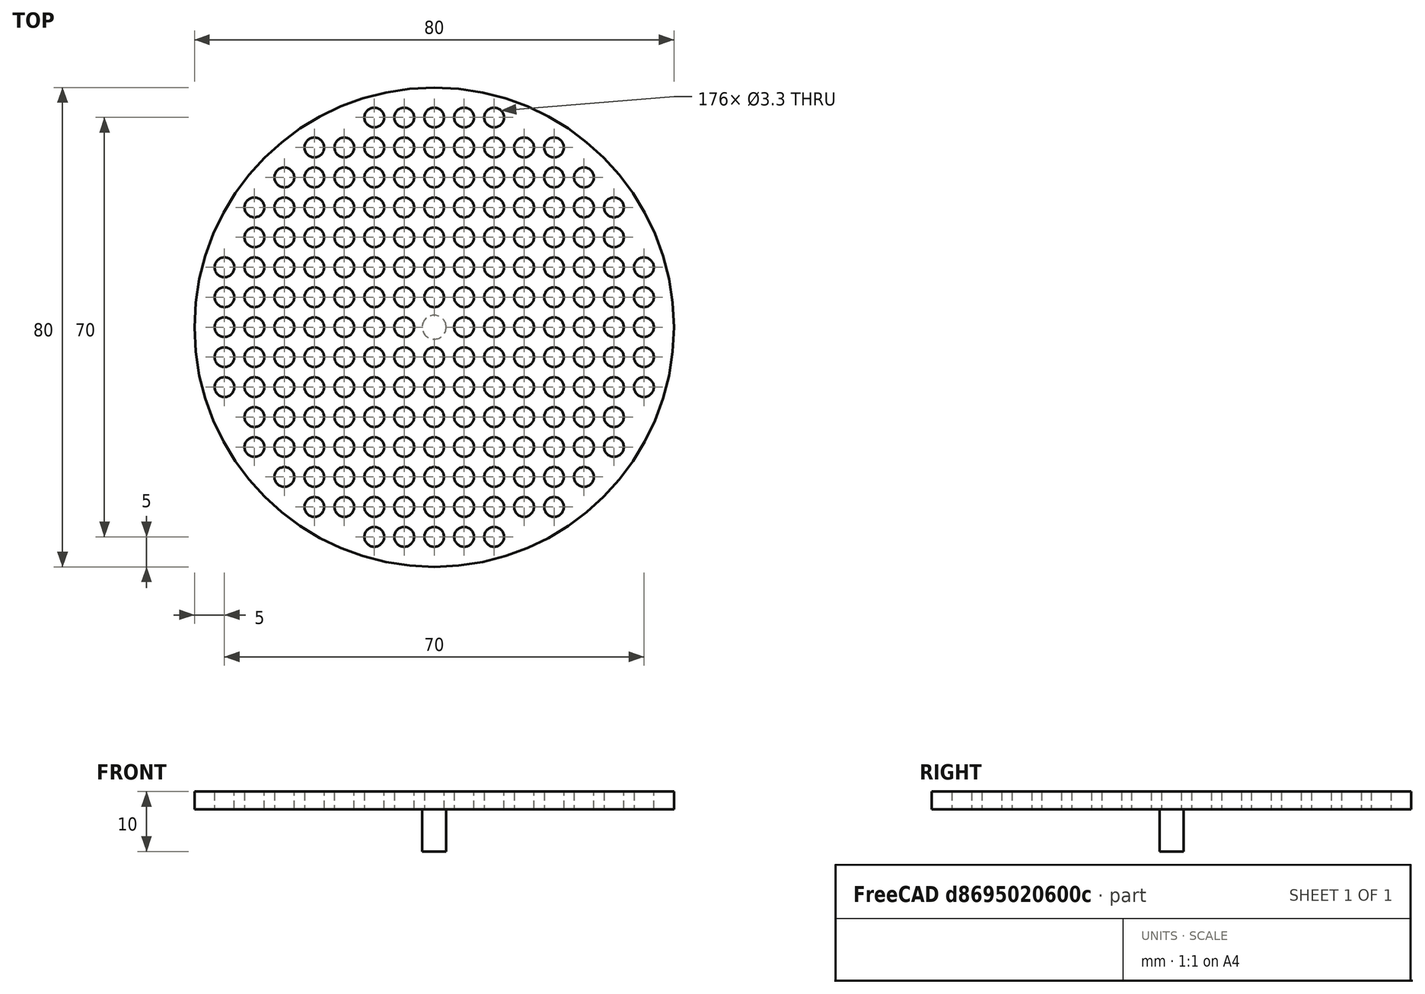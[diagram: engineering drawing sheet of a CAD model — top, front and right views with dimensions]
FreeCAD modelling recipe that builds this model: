
FCSTD DOCUMENT  (FreeCAD 0.21R0.21.2)
Label: XL30SampleholderBreadboard_D80
License: All rights reserved
LicenseURL: https://en.wikipedia.org/wiki/All_rights_reserved
objects: Part::Cylinder×178, Part::MultiFuse×17, TechDraw::DrawViewDimension×7, TechDraw::DrawProjGroupItem×3, Spreadsheet::Sheet×1, Part::Cut×1, TechDraw::DrawSVGTemplate×1, TechDraw::DrawProjGroup×1, TechDraw::DrawPage×1
note: 205 computed .brp shape members not serialized (recipe doc carries the construction recipe); baked Part::Feature solids carry a one-line shape summary decoded from their .brp

FEATURE [Spreadsheet::Sheet] Spreadsheet  label="BreadboardConfig"
  cells = A1='Parameters; A2='Diameter of stage; B2(dia_breadboard)=80; C2='The outer diameter of the breadboard stage; A3='Corehole diameter; B3(screw_corehole)=3.3; C3='Corehole diameter for screws (3.3mm for M4); A4='Plate thickness; B4(t_plate)=3; A5='Hole spacing; B5(screw_spacing)=5
FEATURE [Part::Cylinder] Cylinder
  Angle = 360
  AttacherType = Attacher::AttachEngine3D
  FirstAngle = 0
  Height = 7
  Placement = pos=(0,0,-7) rot=(0,0,1;0rad)
  Radius = 2
  SecondAngle = 0
FEATURE [Part::Cylinder] Cylinder001
  Angle = 360
  AttacherType = Attacher::AttachEngine3D
  FirstAngle = 0
  Height = 3
  Radius = 40
  SecondAngle = 0
  expr: Height = <<BreadboardConfig>>.t_plate
  expr: Radius = <<BreadboardConfig>>.dia_breadboard / 2
FEATURE [Part::MultiFuse] Fusion
  Shapes = -> [Cylinder,Cylinder001]
FEATURE [Part::Cylinder] Cylinder002
  Angle = 360
  AttacherType = Attacher::AttachEngine3D
  FirstAngle = 0
  Height = 3
  Placement = pos=(5,0,0) rot=(0,0,1;0rad)
  Radius = 1.65
  SecondAngle = 0
  expr: .Placement.Base.x = <<BreadboardConfig>>.screw_spacing * 1
  expr: Height = <<BreadboardConfig>>.t_plate
  expr: Radius = <<BreadboardConfig>>.screw_corehole / 2
FEATURE [Part::Cylinder] Cylinder003
  Angle = 360
  AttacherType = Attacher::AttachEngine3D
  FirstAngle = 0
  Height = 3
  Placement = pos=(10,0,0) rot=(0,0,1;0rad)
  Radius = 1.65
  SecondAngle = 0
  expr: .Placement.Base.x = <<BreadboardConfig>>.screw_spacing * 2
  expr: Height = <<BreadboardConfig>>.t_plate
  expr: Radius = <<BreadboardConfig>>.screw_corehole / 2
FEATURE [Part::Cylinder] Cylinder004
  Angle = 360
  AttacherType = Attacher::AttachEngine3D
  FirstAngle = 0
  Height = 3
  Placement = pos=(15,0,0) rot=(0,0,1;0rad)
  Radius = 1.65
  SecondAngle = 0
  expr: .Placement.Base.x = <<BreadboardConfig>>.screw_spacing * 3
  expr: Height = <<BreadboardConfig>>.t_plate
  expr: Radius = <<BreadboardConfig>>.screw_corehole / 2
FEATURE [Part::Cylinder] Cylinder005
  Angle = 360
  AttacherType = Attacher::AttachEngine3D
  FirstAngle = 0
  Height = 3
  Placement = pos=(20,0,0) rot=(0,0,1;0rad)
  Radius = 1.65
  SecondAngle = 0
  expr: .Placement.Base.x = <<BreadboardConfig>>.screw_spacing * 4
  expr: Height = <<BreadboardConfig>>.t_plate
  expr: Radius = <<BreadboardConfig>>.screw_corehole / 2
FEATURE [Part::Cylinder] Cylinder006
  Angle = 360
  AttacherType = Attacher::AttachEngine3D
  FirstAngle = 0
  Height = 3
  Placement = pos=(25,0,0) rot=(0,0,1;0rad)
  Radius = 1.65
  SecondAngle = 0
  expr: .Placement.Base.x = <<BreadboardConfig>>.screw_spacing * 5
  expr: Height = <<BreadboardConfig>>.t_plate
  expr: Radius = <<BreadboardConfig>>.screw_corehole / 2
FEATURE [Part::Cylinder] Cylinder007
  Angle = 360
  AttacherType = Attacher::AttachEngine3D
  FirstAngle = 0
  Height = 3
  Placement = pos=(30,0,0) rot=(0,0,1;0rad)
  Radius = 1.65
  SecondAngle = 0
  expr: .Placement.Base.x = <<BreadboardConfig>>.screw_spacing * 6
  expr: Height = <<BreadboardConfig>>.t_plate
  expr: Radius = <<BreadboardConfig>>.screw_corehole / 2
FEATURE [Part::Cylinder] Cylinder008
  Angle = 360
  AttacherType = Attacher::AttachEngine3D
  FirstAngle = 0
  Height = 3
  Placement = pos=(35,0,0) rot=(0,0,1;0rad)
  Radius = 1.65
  SecondAngle = 0
  expr: .Placement.Base.x = <<BreadboardConfig>>.screw_spacing * 7
  expr: Height = <<BreadboardConfig>>.t_plate
  expr: Radius = <<BreadboardConfig>>.screw_corehole / 2
FEATURE [Part::Cylinder] Cylinder012
  Angle = 360
  AttacherType = Attacher::AttachEngine3D
  FirstAngle = 0
  Height = 3
  Placement = pos=(-5,0,0) rot=(0,0,1;0rad)
  Radius = 1.65
  SecondAngle = 0
  expr: .Placement.Base.x = <<BreadboardConfig>>.screw_spacing * -1
  expr: Height = <<BreadboardConfig>>.t_plate
  expr: Radius = <<BreadboardConfig>>.screw_corehole / 2
FEATURE [Part::Cylinder] Cylinder013
  Angle = 360
  AttacherType = Attacher::AttachEngine3D
  FirstAngle = 0
  Height = 3
  Placement = pos=(-10,0,0) rot=(0,0,1;0rad)
  Radius = 1.65
  SecondAngle = 0
  expr: .Placement.Base.x = <<BreadboardConfig>>.screw_spacing * -2
  expr: Height = <<BreadboardConfig>>.t_plate
  expr: Radius = <<BreadboardConfig>>.screw_corehole / 2
FEATURE [Part::Cylinder] Cylinder014
  Angle = 360
  AttacherType = Attacher::AttachEngine3D
  FirstAngle = 0
  Height = 3
  Placement = pos=(-15,0,0) rot=(0,0,1;0rad)
  Radius = 1.65
  SecondAngle = 0
  expr: .Placement.Base.x = <<BreadboardConfig>>.screw_spacing * -3
  expr: Height = <<BreadboardConfig>>.t_plate
  expr: Radius = <<BreadboardConfig>>.screw_corehole / 2
FEATURE [Part::Cylinder] Cylinder015
  Angle = 360
  AttacherType = Attacher::AttachEngine3D
  FirstAngle = 0
  Height = 3
  Placement = pos=(-20,0,0) rot=(0,0,1;0rad)
  Radius = 1.65
  SecondAngle = 0
  expr: .Placement.Base.x = <<BreadboardConfig>>.screw_spacing * -4
  expr: Height = <<BreadboardConfig>>.t_plate
  expr: Radius = <<BreadboardConfig>>.screw_corehole / 2
FEATURE [Part::Cylinder] Cylinder016
  Angle = 360
  AttacherType = Attacher::AttachEngine3D
  FirstAngle = 0
  Height = 3
  Placement = pos=(-25,0,0) rot=(0,0,1;0rad)
  Radius = 1.65
  SecondAngle = 0
  expr: .Placement.Base.x = <<BreadboardConfig>>.screw_spacing * -5
  expr: Height = <<BreadboardConfig>>.t_plate
  expr: Radius = <<BreadboardConfig>>.screw_corehole / 2
FEATURE [Part::Cylinder] Cylinder017
  Angle = 360
  AttacherType = Attacher::AttachEngine3D
  FirstAngle = 0
  Height = 3
  Placement = pos=(-30,0,0) rot=(0,0,1;0rad)
  Radius = 1.65
  SecondAngle = 0
  expr: .Placement.Base.x = <<BreadboardConfig>>.screw_spacing * -6
  expr: Height = <<BreadboardConfig>>.t_plate
  expr: Radius = <<BreadboardConfig>>.screw_corehole / 2
FEATURE [Part::Cylinder] Cylinder018
  Angle = 360
  AttacherType = Attacher::AttachEngine3D
  FirstAngle = 0
  Height = 3
  Placement = pos=(-35,0,0) rot=(0,0,1;0rad)
  Radius = 1.65
  SecondAngle = 0
  expr: .Placement.Base.x = <<BreadboardConfig>>.screw_spacing * -7
  expr: Height = <<BreadboardConfig>>.t_plate
  expr: Radius = <<BreadboardConfig>>.screw_corehole / 2
FEATURE [Part::MultiFuse] Fusion001
  Shapes = -> [Cylinder018,Cylinder017,Cylinder016,Cylinder015,Cylinder014,Cylinder013,Cylinder012,Cylinder008,Cylinder007,Cylinder006,Cylinder005,Cylinder004,Cylinder003,Cylinder002]
FEATURE [Part::Cylinder] Cylinder022
  Angle = 360
  AttacherType = Attacher::AttachEngine3D
  FirstAngle = 0
  Height = 3
  Placement = pos=(5,0,0) rot=(0,0,1;0rad)
  Radius = 1.65
  SecondAngle = 0
  expr: .Placement.Base.x = <<BreadboardConfig>>.screw_spacing * 1
  expr: Height = <<BreadboardConfig>>.t_plate
  expr: Radius = <<BreadboardConfig>>.screw_corehole / 2
FEATURE [Part::Cylinder] Cylinder023
  Angle = 360
  AttacherType = Attacher::AttachEngine3D
  FirstAngle = 0
  Height = 3
  Placement = pos=(10,0,0) rot=(0,0,1;0rad)
  Radius = 1.65
  SecondAngle = 0
  expr: .Placement.Base.x = <<BreadboardConfig>>.screw_spacing * 2
  expr: Height = <<BreadboardConfig>>.t_plate
  expr: Radius = <<BreadboardConfig>>.screw_corehole / 2
FEATURE [Part::Cylinder] Cylinder024
  Angle = 360
  AttacherType = Attacher::AttachEngine3D
  FirstAngle = 0
  Height = 3
  Placement = pos=(15,0,0) rot=(0,0,1;0rad)
  Radius = 1.65
  SecondAngle = 0
  expr: .Placement.Base.x = <<BreadboardConfig>>.screw_spacing * 3
  expr: Height = <<BreadboardConfig>>.t_plate
  expr: Radius = <<BreadboardConfig>>.screw_corehole / 2
FEATURE [Part::Cylinder] Cylinder032
  Angle = 360
  AttacherType = Attacher::AttachEngine3D
  FirstAngle = 0
  Height = 3
  Placement = pos=(-5,0,0) rot=(0,0,1;0rad)
  Radius = 1.65
  SecondAngle = 0
  expr: .Placement.Base.x = <<BreadboardConfig>>.screw_spacing * -1
  expr: Height = <<BreadboardConfig>>.t_plate
  expr: Radius = <<BreadboardConfig>>.screw_corehole / 2
FEATURE [Part::Cylinder] Cylinder033
  Angle = 360
  AttacherType = Attacher::AttachEngine3D
  FirstAngle = 0
  Height = 3
  Placement = pos=(-10,0,0) rot=(0,0,1;0rad)
  Radius = 1.65
  SecondAngle = 0
  expr: .Placement.Base.x = <<BreadboardConfig>>.screw_spacing * -2
  expr: Height = <<BreadboardConfig>>.t_plate
  expr: Radius = <<BreadboardConfig>>.screw_corehole / 2
FEATURE [Part::Cylinder] Cylinder034
  Angle = 360
  AttacherType = Attacher::AttachEngine3D
  FirstAngle = 0
  Height = 3
  Placement = pos=(-15,0,0) rot=(0,0,1;0rad)
  Radius = 1.65
  SecondAngle = 0
  expr: .Placement.Base.x = <<BreadboardConfig>>.screw_spacing * -3
  expr: Height = <<BreadboardConfig>>.t_plate
  expr: Radius = <<BreadboardConfig>>.screw_corehole / 2
FEATURE [Part::Cylinder] Cylinder042
  Angle = 360
  AttacherType = Attacher::AttachEngine3D
  FirstAngle = 0
  Height = 3
  Radius = 1.65
  SecondAngle = 0
  expr: Height = <<BreadboardConfig>>.t_plate
  expr: Radius = <<BreadboardConfig>>.screw_corehole / 2
FEATURE [Part::Cylinder] Cylinder043
  Angle = 360
  AttacherType = Attacher::AttachEngine3D
  FirstAngle = 0
  Height = 3
  Placement = pos=(5,0,0) rot=(0,0,1;0rad)
  Radius = 1.65
  SecondAngle = 0
  expr: .Placement.Base.x = <<BreadboardConfig>>.screw_spacing * 1
  expr: Height = <<BreadboardConfig>>.t_plate
  expr: Radius = <<BreadboardConfig>>.screw_corehole / 2
FEATURE [Part::Cylinder] Cylinder044
  Angle = 360
  AttacherType = Attacher::AttachEngine3D
  FirstAngle = 0
  Height = 3
  Placement = pos=(10,0,0) rot=(0,0,1;0rad)
  Radius = 1.65
  SecondAngle = 0
  expr: .Placement.Base.x = <<BreadboardConfig>>.screw_spacing * 2
  expr: Height = <<BreadboardConfig>>.t_plate
  expr: Radius = <<BreadboardConfig>>.screw_corehole / 2
FEATURE [Part::Cylinder] Cylinder045
  Angle = 360
  AttacherType = Attacher::AttachEngine3D
  FirstAngle = 0
  Height = 3
  Placement = pos=(15,0,0) rot=(0,0,1;0rad)
  Radius = 1.65
  SecondAngle = 0
  expr: .Placement.Base.x = <<BreadboardConfig>>.screw_spacing * 3
  expr: Height = <<BreadboardConfig>>.t_plate
  expr: Radius = <<BreadboardConfig>>.screw_corehole / 2
FEATURE [Part::Cylinder] Cylinder046
  Angle = 360
  AttacherType = Attacher::AttachEngine3D
  FirstAngle = 0
  Height = 3
  Placement = pos=(20,0,0) rot=(0,0,1;0rad)
  Radius = 1.65
  SecondAngle = 0
  expr: .Placement.Base.x = <<BreadboardConfig>>.screw_spacing * 4
  expr: Height = <<BreadboardConfig>>.t_plate
  expr: Radius = <<BreadboardConfig>>.screw_corehole / 2
FEATURE [Part::Cylinder] Cylinder047
  Angle = 360
  AttacherType = Attacher::AttachEngine3D
  FirstAngle = 0
  Height = 3
  Placement = pos=(25,0,0) rot=(0,0,1;0rad)
  Radius = 1.65
  SecondAngle = 0
  expr: .Placement.Base.x = <<BreadboardConfig>>.screw_spacing * 5
  expr: Height = <<BreadboardConfig>>.t_plate
  expr: Radius = <<BreadboardConfig>>.screw_corehole / 2
FEATURE [Part::Cylinder] Cylinder048
  Angle = 360
  AttacherType = Attacher::AttachEngine3D
  FirstAngle = 0
  Height = 3
  Placement = pos=(30,0,0) rot=(0,0,1;0rad)
  Radius = 1.65
  SecondAngle = 0
  expr: .Placement.Base.x = <<BreadboardConfig>>.screw_spacing * 6
  expr: Height = <<BreadboardConfig>>.t_plate
  expr: Radius = <<BreadboardConfig>>.screw_corehole / 2
FEATURE [Part::Cylinder] Cylinder049
  Angle = 360
  AttacherType = Attacher::AttachEngine3D
  FirstAngle = 0
  Height = 3
  Placement = pos=(35,0,0) rot=(0,0,1;0rad)
  Radius = 1.65
  SecondAngle = 0
  expr: .Placement.Base.x = <<BreadboardConfig>>.screw_spacing * 7
  expr: Height = <<BreadboardConfig>>.t_plate
  expr: Radius = <<BreadboardConfig>>.screw_corehole / 2
FEATURE [Part::Cylinder] Cylinder053
  Angle = 360
  AttacherType = Attacher::AttachEngine3D
  FirstAngle = 0
  Height = 3
  Placement = pos=(-5,0,0) rot=(0,0,1;0rad)
  Radius = 1.65
  SecondAngle = 0
  expr: .Placement.Base.x = <<BreadboardConfig>>.screw_spacing * -1
  expr: Height = <<BreadboardConfig>>.t_plate
  expr: Radius = <<BreadboardConfig>>.screw_corehole / 2
FEATURE [Part::Cylinder] Cylinder054
  Angle = 360
  AttacherType = Attacher::AttachEngine3D
  FirstAngle = 0
  Height = 3
  Placement = pos=(-10,0,0) rot=(0,0,1;0rad)
  Radius = 1.65
  SecondAngle = 0
  expr: .Placement.Base.x = <<BreadboardConfig>>.screw_spacing * -2
  expr: Height = <<BreadboardConfig>>.t_plate
  expr: Radius = <<BreadboardConfig>>.screw_corehole / 2
FEATURE [Part::Cylinder] Cylinder055
  Angle = 360
  AttacherType = Attacher::AttachEngine3D
  FirstAngle = 0
  Height = 3
  Placement = pos=(-15,0,0) rot=(0,0,1;0rad)
  Radius = 1.65
  SecondAngle = 0
  expr: .Placement.Base.x = <<BreadboardConfig>>.screw_spacing * -3
  expr: Height = <<BreadboardConfig>>.t_plate
  expr: Radius = <<BreadboardConfig>>.screw_corehole / 2
FEATURE [Part::Cylinder] Cylinder056
  Angle = 360
  AttacherType = Attacher::AttachEngine3D
  FirstAngle = 0
  Height = 3
  Placement = pos=(-20,0,0) rot=(0,0,1;0rad)
  Radius = 1.65
  SecondAngle = 0
  expr: .Placement.Base.x = <<BreadboardConfig>>.screw_spacing * -4
  expr: Height = <<BreadboardConfig>>.t_plate
  expr: Radius = <<BreadboardConfig>>.screw_corehole / 2
FEATURE [Part::Cylinder] Cylinder057
  Angle = 360
  AttacherType = Attacher::AttachEngine3D
  FirstAngle = 0
  Height = 3
  Placement = pos=(-25,0,0) rot=(0,0,1;0rad)
  Radius = 1.65
  SecondAngle = 0
  expr: .Placement.Base.x = <<BreadboardConfig>>.screw_spacing * -5
  expr: Height = <<BreadboardConfig>>.t_plate
  expr: Radius = <<BreadboardConfig>>.screw_corehole / 2
FEATURE [Part::Cylinder] Cylinder058
  Angle = 360
  AttacherType = Attacher::AttachEngine3D
  FirstAngle = 0
  Height = 3
  Placement = pos=(-30,0,0) rot=(0,0,1;0rad)
  Radius = 1.65
  SecondAngle = 0
  expr: .Placement.Base.x = <<BreadboardConfig>>.screw_spacing * -6
  expr: Height = <<BreadboardConfig>>.t_plate
  expr: Radius = <<BreadboardConfig>>.screw_corehole / 2
FEATURE [Part::Cylinder] Cylinder059
  Angle = 360
  AttacherType = Attacher::AttachEngine3D
  FirstAngle = 0
  Height = 3
  Placement = pos=(-35,0,0) rot=(0,0,1;0rad)
  Radius = 1.65
  SecondAngle = 0
  expr: .Placement.Base.x = <<BreadboardConfig>>.screw_spacing * -7
  expr: Height = <<BreadboardConfig>>.t_plate
  expr: Radius = <<BreadboardConfig>>.screw_corehole / 2
FEATURE [Part::Cylinder] Cylinder063
  Angle = 360
  AttacherType = Attacher::AttachEngine3D
  FirstAngle = 0
  Height = 3
  Radius = 1.65
  SecondAngle = 0
  expr: Height = <<BreadboardConfig>>.t_plate
  expr: Radius = <<BreadboardConfig>>.screw_corehole / 2
FEATURE [Part::MultiFuse] Fusion003
  Placement = pos=(0,10,0) rot=(0,0,1;0rad)
  Shapes = -> [Cylinder059,Cylinder058,Cylinder057,Cylinder056,Cylinder055,Cylinder054,Cylinder053,Cylinder049,Cylinder048,Cylinder047,Cylinder046,Cylinder045,Cylinder044,Cylinder043,Cylinder063]
  expr: .Placement.Base.y = <<BreadboardConfig>>.screw_spacing * 2
FEATURE [Part::Cylinder] Cylinder064
  Angle = 360
  AttacherType = Attacher::AttachEngine3D
  FirstAngle = 0
  Height = 3
  Placement = pos=(5,0,0) rot=(0,0,1;0rad)
  Radius = 1.65
  SecondAngle = 0
  expr: .Placement.Base.x = <<BreadboardConfig>>.screw_spacing * 1
  expr: Height = <<BreadboardConfig>>.t_plate
  expr: Radius = <<BreadboardConfig>>.screw_corehole / 2
FEATURE [Part::Cylinder] Cylinder065
  Angle = 360
  AttacherType = Attacher::AttachEngine3D
  FirstAngle = 0
  Height = 3
  Placement = pos=(10,0,0) rot=(0,0,1;0rad)
  Radius = 1.65
  SecondAngle = 0
  expr: .Placement.Base.x = <<BreadboardConfig>>.screw_spacing * 2
  expr: Height = <<BreadboardConfig>>.t_plate
  expr: Radius = <<BreadboardConfig>>.screw_corehole / 2
FEATURE [Part::Cylinder] Cylinder066
  Angle = 360
  AttacherType = Attacher::AttachEngine3D
  FirstAngle = 0
  Height = 3
  Placement = pos=(15,0,0) rot=(0,0,1;0rad)
  Radius = 1.65
  SecondAngle = 0
  expr: .Placement.Base.x = <<BreadboardConfig>>.screw_spacing * 3
  expr: Height = <<BreadboardConfig>>.t_plate
  expr: Radius = <<BreadboardConfig>>.screw_corehole / 2
FEATURE [Part::Cylinder] Cylinder067
  Angle = 360
  AttacherType = Attacher::AttachEngine3D
  FirstAngle = 0
  Height = 3
  Placement = pos=(20,0,0) rot=(0,0,1;0rad)
  Radius = 1.65
  SecondAngle = 0
  expr: .Placement.Base.x = <<BreadboardConfig>>.screw_spacing * 4
  expr: Height = <<BreadboardConfig>>.t_plate
  expr: Radius = <<BreadboardConfig>>.screw_corehole / 2
FEATURE [Part::Cylinder] Cylinder068
  Angle = 360
  AttacherType = Attacher::AttachEngine3D
  FirstAngle = 0
  Height = 3
  Placement = pos=(25,0,0) rot=(0,0,1;0rad)
  Radius = 1.65
  SecondAngle = 0
  expr: .Placement.Base.x = <<BreadboardConfig>>.screw_spacing * 5
  expr: Height = <<BreadboardConfig>>.t_plate
  expr: Radius = <<BreadboardConfig>>.screw_corehole / 2
FEATURE [Part::Cylinder] Cylinder069
  Angle = 360
  AttacherType = Attacher::AttachEngine3D
  FirstAngle = 0
  Height = 3
  Placement = pos=(30,0,0) rot=(0,0,1;0rad)
  Radius = 1.65
  SecondAngle = 0
  expr: .Placement.Base.x = <<BreadboardConfig>>.screw_spacing * 6
  expr: Height = <<BreadboardConfig>>.t_plate
  expr: Radius = <<BreadboardConfig>>.screw_corehole / 2
FEATURE [Part::Cylinder] Cylinder074
  Angle = 360
  AttacherType = Attacher::AttachEngine3D
  FirstAngle = 0
  Height = 3
  Placement = pos=(-5,0,0) rot=(0,0,1;0rad)
  Radius = 1.65
  SecondAngle = 0
  expr: .Placement.Base.x = <<BreadboardConfig>>.screw_spacing * -1
  expr: Height = <<BreadboardConfig>>.t_plate
  expr: Radius = <<BreadboardConfig>>.screw_corehole / 2
FEATURE [Part::Cylinder] Cylinder075
  Angle = 360
  AttacherType = Attacher::AttachEngine3D
  FirstAngle = 0
  Height = 3
  Placement = pos=(-10,0,0) rot=(0,0,1;0rad)
  Radius = 1.65
  SecondAngle = 0
  expr: .Placement.Base.x = <<BreadboardConfig>>.screw_spacing * -2
  expr: Height = <<BreadboardConfig>>.t_plate
  expr: Radius = <<BreadboardConfig>>.screw_corehole / 2
FEATURE [Part::Cylinder] Cylinder076
  Angle = 360
  AttacherType = Attacher::AttachEngine3D
  FirstAngle = 0
  Height = 3
  Placement = pos=(-15,0,0) rot=(0,0,1;0rad)
  Radius = 1.65
  SecondAngle = 0
  expr: .Placement.Base.x = <<BreadboardConfig>>.screw_spacing * -3
  expr: Height = <<BreadboardConfig>>.t_plate
  expr: Radius = <<BreadboardConfig>>.screw_corehole / 2
FEATURE [Part::Cylinder] Cylinder077
  Angle = 360
  AttacherType = Attacher::AttachEngine3D
  FirstAngle = 0
  Height = 3
  Placement = pos=(-20,0,0) rot=(0,0,1;0rad)
  Radius = 1.65
  SecondAngle = 0
  expr: .Placement.Base.x = <<BreadboardConfig>>.screw_spacing * -4
  expr: Height = <<BreadboardConfig>>.t_plate
  expr: Radius = <<BreadboardConfig>>.screw_corehole / 2
FEATURE [Part::Cylinder] Cylinder078
  Angle = 360
  AttacherType = Attacher::AttachEngine3D
  FirstAngle = 0
  Height = 3
  Placement = pos=(-25,0,0) rot=(0,0,1;0rad)
  Radius = 1.65
  SecondAngle = 0
  expr: .Placement.Base.x = <<BreadboardConfig>>.screw_spacing * -5
  expr: Height = <<BreadboardConfig>>.t_plate
  expr: Radius = <<BreadboardConfig>>.screw_corehole / 2
FEATURE [Part::Cylinder] Cylinder079
  Angle = 360
  AttacherType = Attacher::AttachEngine3D
  FirstAngle = 0
  Height = 3
  Placement = pos=(-30,0,0) rot=(0,0,1;0rad)
  Radius = 1.65
  SecondAngle = 0
  expr: .Placement.Base.x = <<BreadboardConfig>>.screw_spacing * -6
  expr: Height = <<BreadboardConfig>>.t_plate
  expr: Radius = <<BreadboardConfig>>.screw_corehole / 2
FEATURE [Part::Cylinder] Cylinder084
  Angle = 360
  AttacherType = Attacher::AttachEngine3D
  FirstAngle = 0
  Height = 3
  Radius = 1.65
  SecondAngle = 0
  expr: Height = <<BreadboardConfig>>.t_plate
  expr: Radius = <<BreadboardConfig>>.screw_corehole / 2
FEATURE [Part::MultiFuse] Fusion004
  Placement = pos=(0,15,0) rot=(0,0,1;0rad)
  Shapes = -> [Cylinder079,Cylinder078,Cylinder077,Cylinder076,Cylinder075,Cylinder074,Cylinder069,Cylinder068,Cylinder067,Cylinder066,Cylinder065,Cylinder064,Cylinder084]
  expr: .Placement.Base.y = <<BreadboardConfig>>.screw_spacing * 3
FEATURE [Part::Cylinder] Cylinder085
  Angle = 360
  AttacherType = Attacher::AttachEngine3D
  FirstAngle = 0
  Height = 3
  Placement = pos=(5,0,0) rot=(0,0,1;0rad)
  Radius = 1.65
  SecondAngle = 0
  expr: .Placement.Base.x = <<BreadboardConfig>>.screw_spacing * 1
  expr: Height = <<BreadboardConfig>>.t_plate
  expr: Radius = <<BreadboardConfig>>.screw_corehole / 2
FEATURE [Part::Cylinder] Cylinder086
  Angle = 360
  AttacherType = Attacher::AttachEngine3D
  FirstAngle = 0
  Height = 3
  Placement = pos=(10,0,0) rot=(0,0,1;0rad)
  Radius = 1.65
  SecondAngle = 0
  expr: .Placement.Base.x = <<BreadboardConfig>>.screw_spacing * 2
  expr: Height = <<BreadboardConfig>>.t_plate
  expr: Radius = <<BreadboardConfig>>.screw_corehole / 2
FEATURE [Part::Cylinder] Cylinder087
  Angle = 360
  AttacherType = Attacher::AttachEngine3D
  FirstAngle = 0
  Height = 3
  Placement = pos=(15,0,0) rot=(0,0,1;0rad)
  Radius = 1.65
  SecondAngle = 0
  expr: .Placement.Base.x = <<BreadboardConfig>>.screw_spacing * 3
  expr: Height = <<BreadboardConfig>>.t_plate
  expr: Radius = <<BreadboardConfig>>.screw_corehole / 2
FEATURE [Part::Cylinder] Cylinder088
  Angle = 360
  AttacherType = Attacher::AttachEngine3D
  FirstAngle = 0
  Height = 3
  Placement = pos=(20,0,0) rot=(0,0,1;0rad)
  Radius = 1.65
  SecondAngle = 0
  expr: .Placement.Base.x = <<BreadboardConfig>>.screw_spacing * 4
  expr: Height = <<BreadboardConfig>>.t_plate
  expr: Radius = <<BreadboardConfig>>.screw_corehole / 2
FEATURE [Part::Cylinder] Cylinder089
  Angle = 360
  AttacherType = Attacher::AttachEngine3D
  FirstAngle = 0
  Height = 3
  Placement = pos=(25,0,0) rot=(0,0,1;0rad)
  Radius = 1.65
  SecondAngle = 0
  expr: .Placement.Base.x = <<BreadboardConfig>>.screw_spacing * 5
  expr: Height = <<BreadboardConfig>>.t_plate
  expr: Radius = <<BreadboardConfig>>.screw_corehole / 2
FEATURE [Part::Cylinder] Cylinder090
  Angle = 360
  AttacherType = Attacher::AttachEngine3D
  FirstAngle = 0
  Height = 3
  Placement = pos=(30,0,0) rot=(0,0,1;0rad)
  Radius = 1.65
  SecondAngle = 0
  expr: .Placement.Base.x = <<BreadboardConfig>>.screw_spacing * 6
  expr: Height = <<BreadboardConfig>>.t_plate
  expr: Radius = <<BreadboardConfig>>.screw_corehole / 2
FEATURE [Part::Cylinder] Cylinder095
  Angle = 360
  AttacherType = Attacher::AttachEngine3D
  FirstAngle = 0
  Height = 3
  Placement = pos=(-5,0,0) rot=(0,0,1;0rad)
  Radius = 1.65
  SecondAngle = 0
  expr: .Placement.Base.x = <<BreadboardConfig>>.screw_spacing * -1
  expr: Height = <<BreadboardConfig>>.t_plate
  expr: Radius = <<BreadboardConfig>>.screw_corehole / 2
FEATURE [Part::Cylinder] Cylinder096
  Angle = 360
  AttacherType = Attacher::AttachEngine3D
  FirstAngle = 0
  Height = 3
  Placement = pos=(-10,0,0) rot=(0,0,1;0rad)
  Radius = 1.65
  SecondAngle = 0
  expr: .Placement.Base.x = <<BreadboardConfig>>.screw_spacing * -2
  expr: Height = <<BreadboardConfig>>.t_plate
  expr: Radius = <<BreadboardConfig>>.screw_corehole / 2
FEATURE [Part::Cylinder] Cylinder097
  Angle = 360
  AttacherType = Attacher::AttachEngine3D
  FirstAngle = 0
  Height = 3
  Placement = pos=(-15,0,0) rot=(0,0,1;0rad)
  Radius = 1.65
  SecondAngle = 0
  expr: .Placement.Base.x = <<BreadboardConfig>>.screw_spacing * -3
  expr: Height = <<BreadboardConfig>>.t_plate
  expr: Radius = <<BreadboardConfig>>.screw_corehole / 2
FEATURE [Part::Cylinder] Cylinder098
  Angle = 360
  AttacherType = Attacher::AttachEngine3D
  FirstAngle = 0
  Height = 3
  Placement = pos=(-20,0,0) rot=(0,0,1;0rad)
  Radius = 1.65
  SecondAngle = 0
  expr: .Placement.Base.x = <<BreadboardConfig>>.screw_spacing * -4
  expr: Height = <<BreadboardConfig>>.t_plate
  expr: Radius = <<BreadboardConfig>>.screw_corehole / 2
FEATURE [Part::Cylinder] Cylinder099
  Angle = 360
  AttacherType = Attacher::AttachEngine3D
  FirstAngle = 0
  Height = 3
  Placement = pos=(-25,0,0) rot=(0,0,1;0rad)
  Radius = 1.65
  SecondAngle = 0
  expr: .Placement.Base.x = <<BreadboardConfig>>.screw_spacing * -5
  expr: Height = <<BreadboardConfig>>.t_plate
  expr: Radius = <<BreadboardConfig>>.screw_corehole / 2
FEATURE [Part::Cylinder] Cylinder100
  Angle = 360
  AttacherType = Attacher::AttachEngine3D
  FirstAngle = 0
  Height = 3
  Placement = pos=(-30,0,0) rot=(0,0,1;0rad)
  Radius = 1.65
  SecondAngle = 0
  expr: .Placement.Base.x = <<BreadboardConfig>>.screw_spacing * -6
  expr: Height = <<BreadboardConfig>>.t_plate
  expr: Radius = <<BreadboardConfig>>.screw_corehole / 2
FEATURE [Part::Cylinder] Cylinder105
  Angle = 360
  AttacherType = Attacher::AttachEngine3D
  FirstAngle = 0
  Height = 3
  Radius = 1.65
  SecondAngle = 0
  expr: Height = <<BreadboardConfig>>.t_plate
  expr: Radius = <<BreadboardConfig>>.screw_corehole / 2
FEATURE [Part::MultiFuse] Fusion005
  Placement = pos=(0,20,0) rot=(0,0,1;0rad)
  Shapes = -> [Cylinder100,Cylinder099,Cylinder098,Cylinder097,Cylinder096,Cylinder095,Cylinder090,Cylinder089,Cylinder088,Cylinder087,Cylinder086,Cylinder085,Cylinder105]
  expr: .Placement.Base.y = <<BreadboardConfig>>.screw_spacing * 4
FEATURE [Part::Cylinder] Cylinder106
  Angle = 360
  AttacherType = Attacher::AttachEngine3D
  FirstAngle = 0
  Height = 3
  Placement = pos=(5,0,0) rot=(0,0,1;0rad)
  Radius = 1.65
  SecondAngle = 0
  expr: .Placement.Base.x = <<BreadboardConfig>>.screw_spacing * 1
  expr: Height = <<BreadboardConfig>>.t_plate
  expr: Radius = <<BreadboardConfig>>.screw_corehole / 2
FEATURE [Part::Cylinder] Cylinder107
  Angle = 360
  AttacherType = Attacher::AttachEngine3D
  FirstAngle = 0
  Height = 3
  Placement = pos=(10,0,0) rot=(0,0,1;0rad)
  Radius = 1.65
  SecondAngle = 0
  expr: .Placement.Base.x = <<BreadboardConfig>>.screw_spacing * 2
  expr: Height = <<BreadboardConfig>>.t_plate
  expr: Radius = <<BreadboardConfig>>.screw_corehole / 2
FEATURE [Part::Cylinder] Cylinder108
  Angle = 360
  AttacherType = Attacher::AttachEngine3D
  FirstAngle = 0
  Height = 3
  Placement = pos=(15,0,0) rot=(0,0,1;0rad)
  Radius = 1.65
  SecondAngle = 0
  expr: .Placement.Base.x = <<BreadboardConfig>>.screw_spacing * 3
  expr: Height = <<BreadboardConfig>>.t_plate
  expr: Radius = <<BreadboardConfig>>.screw_corehole / 2
FEATURE [Part::Cylinder] Cylinder109
  Angle = 360
  AttacherType = Attacher::AttachEngine3D
  FirstAngle = 0
  Height = 3
  Placement = pos=(20,0,0) rot=(0,0,1;0rad)
  Radius = 1.65
  SecondAngle = 0
  expr: .Placement.Base.x = <<BreadboardConfig>>.screw_spacing * 4
  expr: Height = <<BreadboardConfig>>.t_plate
  expr: Radius = <<BreadboardConfig>>.screw_corehole / 2
FEATURE [Part::Cylinder] Cylinder110
  Angle = 360
  AttacherType = Attacher::AttachEngine3D
  FirstAngle = 0
  Height = 3
  Placement = pos=(25,0,0) rot=(0,0,1;0rad)
  Radius = 1.65
  SecondAngle = 0
  expr: .Placement.Base.x = <<BreadboardConfig>>.screw_spacing * 5
  expr: Height = <<BreadboardConfig>>.t_plate
  expr: Radius = <<BreadboardConfig>>.screw_corehole / 2
FEATURE [Part::Cylinder] Cylinder116
  Angle = 360
  AttacherType = Attacher::AttachEngine3D
  FirstAngle = 0
  Height = 3
  Placement = pos=(-5,0,0) rot=(0,0,1;0rad)
  Radius = 1.65
  SecondAngle = 0
  expr: .Placement.Base.x = <<BreadboardConfig>>.screw_spacing * -1
  expr: Height = <<BreadboardConfig>>.t_plate
  expr: Radius = <<BreadboardConfig>>.screw_corehole / 2
FEATURE [Part::Cylinder] Cylinder117
  Angle = 360
  AttacherType = Attacher::AttachEngine3D
  FirstAngle = 0
  Height = 3
  Placement = pos=(-10,0,0) rot=(0,0,1;0rad)
  Radius = 1.65
  SecondAngle = 0
  expr: .Placement.Base.x = <<BreadboardConfig>>.screw_spacing * -2
  expr: Height = <<BreadboardConfig>>.t_plate
  expr: Radius = <<BreadboardConfig>>.screw_corehole / 2
FEATURE [Part::Cylinder] Cylinder118
  Angle = 360
  AttacherType = Attacher::AttachEngine3D
  FirstAngle = 0
  Height = 3
  Placement = pos=(-15,0,0) rot=(0,0,1;0rad)
  Radius = 1.65
  SecondAngle = 0
  expr: .Placement.Base.x = <<BreadboardConfig>>.screw_spacing * -3
  expr: Height = <<BreadboardConfig>>.t_plate
  expr: Radius = <<BreadboardConfig>>.screw_corehole / 2
FEATURE [Part::Cylinder] Cylinder119
  Angle = 360
  AttacherType = Attacher::AttachEngine3D
  FirstAngle = 0
  Height = 3
  Placement = pos=(-20,0,0) rot=(0,0,1;0rad)
  Radius = 1.65
  SecondAngle = 0
  expr: .Placement.Base.x = <<BreadboardConfig>>.screw_spacing * -4
  expr: Height = <<BreadboardConfig>>.t_plate
  expr: Radius = <<BreadboardConfig>>.screw_corehole / 2
FEATURE [Part::Cylinder] Cylinder120
  Angle = 360
  AttacherType = Attacher::AttachEngine3D
  FirstAngle = 0
  Height = 3
  Placement = pos=(-25,0,0) rot=(0,0,1;0rad)
  Radius = 1.65
  SecondAngle = 0
  expr: .Placement.Base.x = <<BreadboardConfig>>.screw_spacing * -5
  expr: Height = <<BreadboardConfig>>.t_plate
  expr: Radius = <<BreadboardConfig>>.screw_corehole / 2
FEATURE [Part::Cylinder] Cylinder126
  Angle = 360
  AttacherType = Attacher::AttachEngine3D
  FirstAngle = 0
  Height = 3
  Radius = 1.65
  SecondAngle = 0
  expr: Height = <<BreadboardConfig>>.t_plate
  expr: Radius = <<BreadboardConfig>>.screw_corehole / 2
FEATURE [Part::MultiFuse] Fusion006
  Placement = pos=(0,25,0) rot=(0,0,1;0rad)
  Shapes = -> [Cylinder120,Cylinder119,Cylinder118,Cylinder117,Cylinder116,Cylinder110,Cylinder109,Cylinder108,Cylinder107,Cylinder106,Cylinder126]
  expr: .Placement.Base.y = <<BreadboardConfig>>.screw_spacing * 5
FEATURE [Part::Cylinder] Cylinder127
  Angle = 360
  AttacherType = Attacher::AttachEngine3D
  FirstAngle = 0
  Height = 3
  Placement = pos=(5,0,0) rot=(0,0,1;0rad)
  Radius = 1.65
  SecondAngle = 0
  expr: .Placement.Base.x = <<BreadboardConfig>>.screw_spacing * 1
  expr: Height = <<BreadboardConfig>>.t_plate
  expr: Radius = <<BreadboardConfig>>.screw_corehole / 2
FEATURE [Part::Cylinder] Cylinder128
  Angle = 360
  AttacherType = Attacher::AttachEngine3D
  FirstAngle = 0
  Height = 3
  Placement = pos=(10,0,0) rot=(0,0,1;0rad)
  Radius = 1.65
  SecondAngle = 0
  expr: .Placement.Base.x = <<BreadboardConfig>>.screw_spacing * 2
  expr: Height = <<BreadboardConfig>>.t_plate
  expr: Radius = <<BreadboardConfig>>.screw_corehole / 2
FEATURE [Part::Cylinder] Cylinder129
  Angle = 360
  AttacherType = Attacher::AttachEngine3D
  FirstAngle = 0
  Height = 3
  Placement = pos=(15,0,0) rot=(0,0,1;0rad)
  Radius = 1.65
  SecondAngle = 0
  expr: .Placement.Base.x = <<BreadboardConfig>>.screw_spacing * 3
  expr: Height = <<BreadboardConfig>>.t_plate
  expr: Radius = <<BreadboardConfig>>.screw_corehole / 2
FEATURE [Part::Cylinder] Cylinder130
  Angle = 360
  AttacherType = Attacher::AttachEngine3D
  FirstAngle = 0
  Height = 3
  Placement = pos=(20,0,0) rot=(0,0,1;0rad)
  Radius = 1.65
  SecondAngle = 0
  expr: .Placement.Base.x = <<BreadboardConfig>>.screw_spacing * 4
  expr: Height = <<BreadboardConfig>>.t_plate
  expr: Radius = <<BreadboardConfig>>.screw_corehole / 2
FEATURE [Part::Cylinder] Cylinder137
  Angle = 360
  AttacherType = Attacher::AttachEngine3D
  FirstAngle = 0
  Height = 3
  Placement = pos=(-5,0,0) rot=(0,0,1;0rad)
  Radius = 1.65
  SecondAngle = 0
  expr: .Placement.Base.x = <<BreadboardConfig>>.screw_spacing * -1
  expr: Height = <<BreadboardConfig>>.t_plate
  expr: Radius = <<BreadboardConfig>>.screw_corehole / 2
FEATURE [Part::Cylinder] Cylinder138
  Angle = 360
  AttacherType = Attacher::AttachEngine3D
  FirstAngle = 0
  Height = 3
  Placement = pos=(-10,0,0) rot=(0,0,1;0rad)
  Radius = 1.65
  SecondAngle = 0
  expr: .Placement.Base.x = <<BreadboardConfig>>.screw_spacing * -2
  expr: Height = <<BreadboardConfig>>.t_plate
  expr: Radius = <<BreadboardConfig>>.screw_corehole / 2
FEATURE [Part::Cylinder] Cylinder139
  Angle = 360
  AttacherType = Attacher::AttachEngine3D
  FirstAngle = 0
  Height = 3
  Placement = pos=(-15,0,0) rot=(0,0,1;0rad)
  Radius = 1.65
  SecondAngle = 0
  expr: .Placement.Base.x = <<BreadboardConfig>>.screw_spacing * -3
  expr: Height = <<BreadboardConfig>>.t_plate
  expr: Radius = <<BreadboardConfig>>.screw_corehole / 2
FEATURE [Part::Cylinder] Cylinder140
  Angle = 360
  AttacherType = Attacher::AttachEngine3D
  FirstAngle = 0
  Height = 3
  Placement = pos=(-20,0,0) rot=(0,0,1;0rad)
  Radius = 1.65
  SecondAngle = 0
  expr: .Placement.Base.x = <<BreadboardConfig>>.screw_spacing * -4
  expr: Height = <<BreadboardConfig>>.t_plate
  expr: Radius = <<BreadboardConfig>>.screw_corehole / 2
FEATURE [Part::Cylinder] Cylinder147
  Angle = 360
  AttacherType = Attacher::AttachEngine3D
  FirstAngle = 0
  Height = 3
  Radius = 1.65
  SecondAngle = 0
  expr: Height = <<BreadboardConfig>>.t_plate
  expr: Radius = <<BreadboardConfig>>.screw_corehole / 2
FEATURE [Part::MultiFuse] Fusion007
  Placement = pos=(0,30,0) rot=(0,0,1;0rad)
  Shapes = -> [Cylinder140,Cylinder139,Cylinder138,Cylinder137,Cylinder130,Cylinder129,Cylinder128,Cylinder127,Cylinder147]
  expr: .Placement.Base.y = <<BreadboardConfig>>.screw_spacing * 6
FEATURE [Part::Cylinder] Cylinder148
  Angle = 360
  AttacherType = Attacher::AttachEngine3D
  FirstAngle = 0
  Height = 3
  Placement = pos=(5,0,0) rot=(0,0,1;0rad)
  Radius = 1.65
  SecondAngle = 0
  expr: .Placement.Base.x = <<BreadboardConfig>>.screw_spacing * 1
  expr: Height = <<BreadboardConfig>>.t_plate
  expr: Radius = <<BreadboardConfig>>.screw_corehole / 2
FEATURE [Part::Cylinder] Cylinder149
  Angle = 360
  AttacherType = Attacher::AttachEngine3D
  FirstAngle = 0
  Height = 3
  Placement = pos=(10,0,0) rot=(0,0,1;0rad)
  Radius = 1.65
  SecondAngle = 0
  expr: .Placement.Base.x = <<BreadboardConfig>>.screw_spacing * 2
  expr: Height = <<BreadboardConfig>>.t_plate
  expr: Radius = <<BreadboardConfig>>.screw_corehole / 2
FEATURE [Part::Cylinder] Cylinder158
  Angle = 360
  AttacherType = Attacher::AttachEngine3D
  FirstAngle = 0
  Height = 3
  Placement = pos=(-5,0,0) rot=(0,0,1;0rad)
  Radius = 1.65
  SecondAngle = 0
  expr: .Placement.Base.x = <<BreadboardConfig>>.screw_spacing * -1
  expr: Height = <<BreadboardConfig>>.t_plate
  expr: Radius = <<BreadboardConfig>>.screw_corehole / 2
FEATURE [Part::Cylinder] Cylinder159
  Angle = 360
  AttacherType = Attacher::AttachEngine3D
  FirstAngle = 0
  Height = 3
  Placement = pos=(-10,0,0) rot=(0,0,1;0rad)
  Radius = 1.65
  SecondAngle = 0
  expr: .Placement.Base.x = <<BreadboardConfig>>.screw_spacing * -2
  expr: Height = <<BreadboardConfig>>.t_plate
  expr: Radius = <<BreadboardConfig>>.screw_corehole / 2
FEATURE [Part::Cylinder] Cylinder168
  Angle = 360
  AttacherType = Attacher::AttachEngine3D
  FirstAngle = 0
  Height = 3
  Radius = 1.65
  SecondAngle = 0
  expr: Height = <<BreadboardConfig>>.t_plate
  expr: Radius = <<BreadboardConfig>>.screw_corehole / 2
FEATURE [Part::MultiFuse] Fusion008
  Placement = pos=(0,35,0) rot=(0,0,1;0rad)
  Shapes = -> [Cylinder159,Cylinder158,Cylinder149,Cylinder148,Cylinder168]
  expr: .Placement.Base.y = <<BreadboardConfig>>.screw_spacing * 7
FEATURE [Part::Cylinder] Cylinder232
  Angle = 360
  AttacherType = Attacher::AttachEngine3D
  FirstAngle = 0
  Height = 3
  Placement = pos=(5,0,0) rot=(0,0,1;0rad)
  Radius = 1.65
  SecondAngle = 0
  expr: .Placement.Base.x = <<BreadboardConfig>>.screw_spacing * 1
  expr: Height = <<BreadboardConfig>>.t_plate
  expr: Radius = <<BreadboardConfig>>.screw_corehole / 2
FEATURE [Part::Cylinder] Cylinder233
  Angle = 360
  AttacherType = Attacher::AttachEngine3D
  FirstAngle = 0
  Height = 3
  Placement = pos=(10,0,0) rot=(0,0,1;0rad)
  Radius = 1.65
  SecondAngle = 0
  expr: .Placement.Base.x = <<BreadboardConfig>>.screw_spacing * 2
  expr: Height = <<BreadboardConfig>>.t_plate
  expr: Radius = <<BreadboardConfig>>.screw_corehole / 2
FEATURE [Part::Cylinder] Cylinder234
  Angle = 360
  AttacherType = Attacher::AttachEngine3D
  FirstAngle = 0
  Height = 3
  Placement = pos=(15,0,0) rot=(0,0,1;0rad)
  Radius = 1.65
  SecondAngle = 0
  expr: .Placement.Base.x = <<BreadboardConfig>>.screw_spacing * 3
  expr: Height = <<BreadboardConfig>>.t_plate
  expr: Radius = <<BreadboardConfig>>.screw_corehole / 2
FEATURE [Part::Cylinder] Cylinder235
  Angle = 360
  AttacherType = Attacher::AttachEngine3D
  FirstAngle = 0
  Height = 3
  Placement = pos=(20,0,0) rot=(0,0,1;0rad)
  Radius = 1.65
  SecondAngle = 0
  expr: .Placement.Base.x = <<BreadboardConfig>>.screw_spacing * 4
  expr: Height = <<BreadboardConfig>>.t_plate
  expr: Radius = <<BreadboardConfig>>.screw_corehole / 2
FEATURE [Part::Cylinder] Cylinder236
  Angle = 360
  AttacherType = Attacher::AttachEngine3D
  FirstAngle = 0
  Height = 3
  Placement = pos=(25,0,0) rot=(0,0,1;0rad)
  Radius = 1.65
  SecondAngle = 0
  expr: .Placement.Base.x = <<BreadboardConfig>>.screw_spacing * 5
  expr: Height = <<BreadboardConfig>>.t_plate
  expr: Radius = <<BreadboardConfig>>.screw_corehole / 2
FEATURE [Part::Cylinder] Cylinder237
  Angle = 360
  AttacherType = Attacher::AttachEngine3D
  FirstAngle = 0
  Height = 3
  Placement = pos=(30,0,0) rot=(0,0,1;0rad)
  Radius = 1.65
  SecondAngle = 0
  expr: .Placement.Base.x = <<BreadboardConfig>>.screw_spacing * 6
  expr: Height = <<BreadboardConfig>>.t_plate
  expr: Radius = <<BreadboardConfig>>.screw_corehole / 2
FEATURE [Part::Cylinder] Cylinder238
  Angle = 360
  AttacherType = Attacher::AttachEngine3D
  FirstAngle = 0
  Height = 3
  Placement = pos=(35,0,0) rot=(0,0,1;0rad)
  Radius = 1.65
  SecondAngle = 0
  expr: .Placement.Base.x = <<BreadboardConfig>>.screw_spacing * 7
  expr: Height = <<BreadboardConfig>>.t_plate
  expr: Radius = <<BreadboardConfig>>.screw_corehole / 2
FEATURE [Part::Cylinder] Cylinder242
  Angle = 360
  AttacherType = Attacher::AttachEngine3D
  FirstAngle = 0
  Height = 3
  Placement = pos=(-5,0,0) rot=(0,0,1;0rad)
  Radius = 1.65
  SecondAngle = 0
  expr: .Placement.Base.x = <<BreadboardConfig>>.screw_spacing * -1
  expr: Height = <<BreadboardConfig>>.t_plate
  expr: Radius = <<BreadboardConfig>>.screw_corehole / 2
FEATURE [Part::Cylinder] Cylinder243
  Angle = 360
  AttacherType = Attacher::AttachEngine3D
  FirstAngle = 0
  Height = 3
  Placement = pos=(-10,0,0) rot=(0,0,1;0rad)
  Radius = 1.65
  SecondAngle = 0
  expr: .Placement.Base.x = <<BreadboardConfig>>.screw_spacing * -2
  expr: Height = <<BreadboardConfig>>.t_plate
  expr: Radius = <<BreadboardConfig>>.screw_corehole / 2
FEATURE [Part::Cylinder] Cylinder244
  Angle = 360
  AttacherType = Attacher::AttachEngine3D
  FirstAngle = 0
  Height = 3
  Placement = pos=(-15,0,0) rot=(0,0,1;0rad)
  Radius = 1.65
  SecondAngle = 0
  expr: .Placement.Base.x = <<BreadboardConfig>>.screw_spacing * -3
  expr: Height = <<BreadboardConfig>>.t_plate
  expr: Radius = <<BreadboardConfig>>.screw_corehole / 2
FEATURE [Part::Cylinder] Cylinder245
  Angle = 360
  AttacherType = Attacher::AttachEngine3D
  FirstAngle = 0
  Height = 3
  Placement = pos=(-20,0,0) rot=(0,0,1;0rad)
  Radius = 1.65
  SecondAngle = 0
  expr: .Placement.Base.x = <<BreadboardConfig>>.screw_spacing * -4
  expr: Height = <<BreadboardConfig>>.t_plate
  expr: Radius = <<BreadboardConfig>>.screw_corehole / 2
FEATURE [Part::Cylinder] Cylinder246
  Angle = 360
  AttacherType = Attacher::AttachEngine3D
  FirstAngle = 0
  Height = 3
  Placement = pos=(-25,0,0) rot=(0,0,1;0rad)
  Radius = 1.65
  SecondAngle = 0
  expr: .Placement.Base.x = <<BreadboardConfig>>.screw_spacing * -5
  expr: Height = <<BreadboardConfig>>.t_plate
  expr: Radius = <<BreadboardConfig>>.screw_corehole / 2
FEATURE [Part::Cylinder] Cylinder247
  Angle = 360
  AttacherType = Attacher::AttachEngine3D
  FirstAngle = 0
  Height = 3
  Placement = pos=(-30,0,0) rot=(0,0,1;0rad)
  Radius = 1.65
  SecondAngle = 0
  expr: .Placement.Base.x = <<BreadboardConfig>>.screw_spacing * -6
  expr: Height = <<BreadboardConfig>>.t_plate
  expr: Radius = <<BreadboardConfig>>.screw_corehole / 2
FEATURE [Part::Cylinder] Cylinder248
  Angle = 360
  AttacherType = Attacher::AttachEngine3D
  FirstAngle = 0
  Height = 3
  Placement = pos=(-35,0,0) rot=(0,0,1;0rad)
  Radius = 1.65
  SecondAngle = 0
  expr: .Placement.Base.x = <<BreadboardConfig>>.screw_spacing * -7
  expr: Height = <<BreadboardConfig>>.t_plate
  expr: Radius = <<BreadboardConfig>>.screw_corehole / 2
FEATURE [Part::Cylinder] Cylinder252
  Angle = 360
  AttacherType = Attacher::AttachEngine3D
  FirstAngle = 0
  Height = 3
  Radius = 1.65
  SecondAngle = 0
  expr: Height = <<BreadboardConfig>>.t_plate
  expr: Radius = <<BreadboardConfig>>.screw_corehole / 2
FEATURE [Part::MultiFuse] Fusion012
  Placement = pos=(0,-5,0) rot=(0,0,1;0rad)
  Shapes = -> [Cylinder248,Cylinder247,Cylinder246,Cylinder245,Cylinder244,Cylinder243,Cylinder242,Cylinder238,Cylinder237,Cylinder236,Cylinder235,Cylinder234,Cylinder233,Cylinder232,Cylinder252]
  expr: .Placement.Base.y = <<BreadboardConfig>>.screw_spacing * -1
FEATURE [Part::Cylinder] Cylinder253
  Angle = 360
  AttacherType = Attacher::AttachEngine3D
  FirstAngle = 0
  Height = 3
  Placement = pos=(5,0,0) rot=(0,0,1;0rad)
  Radius = 1.65
  SecondAngle = 0
  expr: .Placement.Base.x = <<BreadboardConfig>>.screw_spacing * 1
  expr: Height = <<BreadboardConfig>>.t_plate
  expr: Radius = <<BreadboardConfig>>.screw_corehole / 2
FEATURE [Part::Cylinder] Cylinder254
  Angle = 360
  AttacherType = Attacher::AttachEngine3D
  FirstAngle = 0
  Height = 3
  Placement = pos=(10,0,0) rot=(0,0,1;0rad)
  Radius = 1.65
  SecondAngle = 0
  expr: .Placement.Base.x = <<BreadboardConfig>>.screw_spacing * 2
  expr: Height = <<BreadboardConfig>>.t_plate
  expr: Radius = <<BreadboardConfig>>.screw_corehole / 2
FEATURE [Part::Cylinder] Cylinder255
  Angle = 360
  AttacherType = Attacher::AttachEngine3D
  FirstAngle = 0
  Height = 3
  Placement = pos=(15,0,0) rot=(0,0,1;0rad)
  Radius = 1.65
  SecondAngle = 0
  expr: .Placement.Base.x = <<BreadboardConfig>>.screw_spacing * 3
  expr: Height = <<BreadboardConfig>>.t_plate
  expr: Radius = <<BreadboardConfig>>.screw_corehole / 2
FEATURE [Part::Cylinder] Cylinder256
  Angle = 360
  AttacherType = Attacher::AttachEngine3D
  FirstAngle = 0
  Height = 3
  Placement = pos=(20,0,0) rot=(0,0,1;0rad)
  Radius = 1.65
  SecondAngle = 0
  expr: .Placement.Base.x = <<BreadboardConfig>>.screw_spacing * 4
  expr: Height = <<BreadboardConfig>>.t_plate
  expr: Radius = <<BreadboardConfig>>.screw_corehole / 2
FEATURE [Part::Cylinder] Cylinder257
  Angle = 360
  AttacherType = Attacher::AttachEngine3D
  FirstAngle = 0
  Height = 3
  Placement = pos=(25,0,0) rot=(0,0,1;0rad)
  Radius = 1.65
  SecondAngle = 0
  expr: .Placement.Base.x = <<BreadboardConfig>>.screw_spacing * 5
  expr: Height = <<BreadboardConfig>>.t_plate
  expr: Radius = <<BreadboardConfig>>.screw_corehole / 2
FEATURE [Part::Cylinder] Cylinder258
  Angle = 360
  AttacherType = Attacher::AttachEngine3D
  FirstAngle = 0
  Height = 3
  Placement = pos=(30,0,0) rot=(0,0,1;0rad)
  Radius = 1.65
  SecondAngle = 0
  expr: .Placement.Base.x = <<BreadboardConfig>>.screw_spacing * 6
  expr: Height = <<BreadboardConfig>>.t_plate
  expr: Radius = <<BreadboardConfig>>.screw_corehole / 2
FEATURE [Part::Cylinder] Cylinder259
  Angle = 360
  AttacherType = Attacher::AttachEngine3D
  FirstAngle = 0
  Height = 3
  Placement = pos=(35,0,0) rot=(0,0,1;0rad)
  Radius = 1.65
  SecondAngle = 0
  expr: .Placement.Base.x = <<BreadboardConfig>>.screw_spacing * 7
  expr: Height = <<BreadboardConfig>>.t_plate
  expr: Radius = <<BreadboardConfig>>.screw_corehole / 2
FEATURE [Part::Cylinder] Cylinder263
  Angle = 360
  AttacherType = Attacher::AttachEngine3D
  FirstAngle = 0
  Height = 3
  Placement = pos=(-5,0,0) rot=(0,0,1;0rad)
  Radius = 1.65
  SecondAngle = 0
  expr: .Placement.Base.x = <<BreadboardConfig>>.screw_spacing * -1
  expr: Height = <<BreadboardConfig>>.t_plate
  expr: Radius = <<BreadboardConfig>>.screw_corehole / 2
FEATURE [Part::Cylinder] Cylinder264
  Angle = 360
  AttacherType = Attacher::AttachEngine3D
  FirstAngle = 0
  Height = 3
  Placement = pos=(-10,0,0) rot=(0,0,1;0rad)
  Radius = 1.65
  SecondAngle = 0
  expr: .Placement.Base.x = <<BreadboardConfig>>.screw_spacing * -2
  expr: Height = <<BreadboardConfig>>.t_plate
  expr: Radius = <<BreadboardConfig>>.screw_corehole / 2
FEATURE [Part::Cylinder] Cylinder265
  Angle = 360
  AttacherType = Attacher::AttachEngine3D
  FirstAngle = 0
  Height = 3
  Placement = pos=(-15,0,0) rot=(0,0,1;0rad)
  Radius = 1.65
  SecondAngle = 0
  expr: .Placement.Base.x = <<BreadboardConfig>>.screw_spacing * -3
  expr: Height = <<BreadboardConfig>>.t_plate
  expr: Radius = <<BreadboardConfig>>.screw_corehole / 2
FEATURE [Part::Cylinder] Cylinder266
  Angle = 360
  AttacherType = Attacher::AttachEngine3D
  FirstAngle = 0
  Height = 3
  Placement = pos=(-20,0,0) rot=(0,0,1;0rad)
  Radius = 1.65
  SecondAngle = 0
  expr: .Placement.Base.x = <<BreadboardConfig>>.screw_spacing * -4
  expr: Height = <<BreadboardConfig>>.t_plate
  expr: Radius = <<BreadboardConfig>>.screw_corehole / 2
FEATURE [Part::Cylinder] Cylinder267
  Angle = 360
  AttacherType = Attacher::AttachEngine3D
  FirstAngle = 0
  Height = 3
  Placement = pos=(-25,0,0) rot=(0,0,1;0rad)
  Radius = 1.65
  SecondAngle = 0
  expr: .Placement.Base.x = <<BreadboardConfig>>.screw_spacing * -5
  expr: Height = <<BreadboardConfig>>.t_plate
  expr: Radius = <<BreadboardConfig>>.screw_corehole / 2
FEATURE [Part::Cylinder] Cylinder268
  Angle = 360
  AttacherType = Attacher::AttachEngine3D
  FirstAngle = 0
  Height = 3
  Placement = pos=(-30,0,0) rot=(0,0,1;0rad)
  Radius = 1.65
  SecondAngle = 0
  expr: .Placement.Base.x = <<BreadboardConfig>>.screw_spacing * -6
  expr: Height = <<BreadboardConfig>>.t_plate
  expr: Radius = <<BreadboardConfig>>.screw_corehole / 2
FEATURE [Part::Cylinder] Cylinder269
  Angle = 360
  AttacherType = Attacher::AttachEngine3D
  FirstAngle = 0
  Height = 3
  Placement = pos=(-35,0,0) rot=(0,0,1;0rad)
  Radius = 1.65
  SecondAngle = 0
  expr: .Placement.Base.x = <<BreadboardConfig>>.screw_spacing * -7
  expr: Height = <<BreadboardConfig>>.t_plate
  expr: Radius = <<BreadboardConfig>>.screw_corehole / 2
FEATURE [Part::Cylinder] Cylinder273
  Angle = 360
  AttacherType = Attacher::AttachEngine3D
  FirstAngle = 0
  Height = 3
  Radius = 1.65
  SecondAngle = 0
  expr: Height = <<BreadboardConfig>>.t_plate
  expr: Radius = <<BreadboardConfig>>.screw_corehole / 2
FEATURE [Part::MultiFuse] Fusion013
  Placement = pos=(0,-10,0) rot=(0,0,1;0rad)
  Shapes = -> [Cylinder269,Cylinder268,Cylinder267,Cylinder266,Cylinder265,Cylinder264,Cylinder263,Cylinder259,Cylinder258,Cylinder257,Cylinder256,Cylinder255,Cylinder254,Cylinder253,Cylinder273]
  expr: .Placement.Base.y = <<BreadboardConfig>>.screw_spacing * -2
FEATURE [Part::Cylinder] Cylinder274
  Angle = 360
  AttacherType = Attacher::AttachEngine3D
  FirstAngle = 0
  Height = 3
  Placement = pos=(5,0,0) rot=(0,0,1;0rad)
  Radius = 1.65
  SecondAngle = 0
  expr: .Placement.Base.x = <<BreadboardConfig>>.screw_spacing * 1
  expr: Height = <<BreadboardConfig>>.t_plate
  expr: Radius = <<BreadboardConfig>>.screw_corehole / 2
FEATURE [Part::Cylinder] Cylinder275
  Angle = 360
  AttacherType = Attacher::AttachEngine3D
  FirstAngle = 0
  Height = 3
  Placement = pos=(10,0,0) rot=(0,0,1;0rad)
  Radius = 1.65
  SecondAngle = 0
  expr: .Placement.Base.x = <<BreadboardConfig>>.screw_spacing * 2
  expr: Height = <<BreadboardConfig>>.t_plate
  expr: Radius = <<BreadboardConfig>>.screw_corehole / 2
FEATURE [Part::Cylinder] Cylinder276
  Angle = 360
  AttacherType = Attacher::AttachEngine3D
  FirstAngle = 0
  Height = 3
  Placement = pos=(15,0,0) rot=(0,0,1;0rad)
  Radius = 1.65
  SecondAngle = 0
  expr: .Placement.Base.x = <<BreadboardConfig>>.screw_spacing * 3
  expr: Height = <<BreadboardConfig>>.t_plate
  expr: Radius = <<BreadboardConfig>>.screw_corehole / 2
FEATURE [Part::Cylinder] Cylinder277
  Angle = 360
  AttacherType = Attacher::AttachEngine3D
  FirstAngle = 0
  Height = 3
  Placement = pos=(20,0,0) rot=(0,0,1;0rad)
  Radius = 1.65
  SecondAngle = 0
  expr: .Placement.Base.x = <<BreadboardConfig>>.screw_spacing * 4
  expr: Height = <<BreadboardConfig>>.t_plate
  expr: Radius = <<BreadboardConfig>>.screw_corehole / 2
FEATURE [Part::Cylinder] Cylinder278
  Angle = 360
  AttacherType = Attacher::AttachEngine3D
  FirstAngle = 0
  Height = 3
  Placement = pos=(25,0,0) rot=(0,0,1;0rad)
  Radius = 1.65
  SecondAngle = 0
  expr: .Placement.Base.x = <<BreadboardConfig>>.screw_spacing * 5
  expr: Height = <<BreadboardConfig>>.t_plate
  expr: Radius = <<BreadboardConfig>>.screw_corehole / 2
FEATURE [Part::Cylinder] Cylinder279
  Angle = 360
  AttacherType = Attacher::AttachEngine3D
  FirstAngle = 0
  Height = 3
  Placement = pos=(30,0,0) rot=(0,0,1;0rad)
  Radius = 1.65
  SecondAngle = 0
  expr: .Placement.Base.x = <<BreadboardConfig>>.screw_spacing * 6
  expr: Height = <<BreadboardConfig>>.t_plate
  expr: Radius = <<BreadboardConfig>>.screw_corehole / 2
FEATURE [Part::Cylinder] Cylinder284
  Angle = 360
  AttacherType = Attacher::AttachEngine3D
  FirstAngle = 0
  Height = 3
  Placement = pos=(-5,0,0) rot=(0,0,1;0rad)
  Radius = 1.65
  SecondAngle = 0
  expr: .Placement.Base.x = <<BreadboardConfig>>.screw_spacing * -1
  expr: Height = <<BreadboardConfig>>.t_plate
  expr: Radius = <<BreadboardConfig>>.screw_corehole / 2
FEATURE [Part::Cylinder] Cylinder285
  Angle = 360
  AttacherType = Attacher::AttachEngine3D
  FirstAngle = 0
  Height = 3
  Placement = pos=(-10,0,0) rot=(0,0,1;0rad)
  Radius = 1.65
  SecondAngle = 0
  expr: .Placement.Base.x = <<BreadboardConfig>>.screw_spacing * -2
  expr: Height = <<BreadboardConfig>>.t_plate
  expr: Radius = <<BreadboardConfig>>.screw_corehole / 2
FEATURE [Part::Cylinder] Cylinder286
  Angle = 360
  AttacherType = Attacher::AttachEngine3D
  FirstAngle = 0
  Height = 3
  Placement = pos=(-15,0,0) rot=(0,0,1;0rad)
  Radius = 1.65
  SecondAngle = 0
  expr: .Placement.Base.x = <<BreadboardConfig>>.screw_spacing * -3
  expr: Height = <<BreadboardConfig>>.t_plate
  expr: Radius = <<BreadboardConfig>>.screw_corehole / 2
FEATURE [Part::Cylinder] Cylinder287
  Angle = 360
  AttacherType = Attacher::AttachEngine3D
  FirstAngle = 0
  Height = 3
  Placement = pos=(-20,0,0) rot=(0,0,1;0rad)
  Radius = 1.65
  SecondAngle = 0
  expr: .Placement.Base.x = <<BreadboardConfig>>.screw_spacing * -4
  expr: Height = <<BreadboardConfig>>.t_plate
  expr: Radius = <<BreadboardConfig>>.screw_corehole / 2
FEATURE [Part::Cylinder] Cylinder288
  Angle = 360
  AttacherType = Attacher::AttachEngine3D
  FirstAngle = 0
  Height = 3
  Placement = pos=(-25,0,0) rot=(0,0,1;0rad)
  Radius = 1.65
  SecondAngle = 0
  expr: .Placement.Base.x = <<BreadboardConfig>>.screw_spacing * -5
  expr: Height = <<BreadboardConfig>>.t_plate
  expr: Radius = <<BreadboardConfig>>.screw_corehole / 2
FEATURE [Part::Cylinder] Cylinder289
  Angle = 360
  AttacherType = Attacher::AttachEngine3D
  FirstAngle = 0
  Height = 3
  Placement = pos=(-30,0,0) rot=(0,0,1;0rad)
  Radius = 1.65
  SecondAngle = 0
  expr: .Placement.Base.x = <<BreadboardConfig>>.screw_spacing * -6
  expr: Height = <<BreadboardConfig>>.t_plate
  expr: Radius = <<BreadboardConfig>>.screw_corehole / 2
FEATURE [Part::Cylinder] Cylinder294
  Angle = 360
  AttacherType = Attacher::AttachEngine3D
  FirstAngle = 0
  Height = 3
  Radius = 1.65
  SecondAngle = 0
  expr: Height = <<BreadboardConfig>>.t_plate
  expr: Radius = <<BreadboardConfig>>.screw_corehole / 2
FEATURE [Part::MultiFuse] Fusion014
  Placement = pos=(0,-15,0) rot=(0,0,1;0rad)
  Shapes = -> [Cylinder289,Cylinder288,Cylinder287,Cylinder286,Cylinder285,Cylinder284,Cylinder279,Cylinder278,Cylinder277,Cylinder276,Cylinder275,Cylinder274,Cylinder294]
  expr: .Placement.Base.y = <<BreadboardConfig>>.screw_spacing * -3
FEATURE [Part::Cylinder] Cylinder295
  Angle = 360
  AttacherType = Attacher::AttachEngine3D
  FirstAngle = 0
  Height = 3
  Placement = pos=(5,0,0) rot=(0,0,1;0rad)
  Radius = 1.65
  SecondAngle = 0
  expr: .Placement.Base.x = <<BreadboardConfig>>.screw_spacing * 1
  expr: Height = <<BreadboardConfig>>.t_plate
  expr: Radius = <<BreadboardConfig>>.screw_corehole / 2
FEATURE [Part::Cylinder] Cylinder296
  Angle = 360
  AttacherType = Attacher::AttachEngine3D
  FirstAngle = 0
  Height = 3
  Placement = pos=(10,0,0) rot=(0,0,1;0rad)
  Radius = 1.65
  SecondAngle = 0
  expr: .Placement.Base.x = <<BreadboardConfig>>.screw_spacing * 2
  expr: Height = <<BreadboardConfig>>.t_plate
  expr: Radius = <<BreadboardConfig>>.screw_corehole / 2
FEATURE [Part::Cylinder] Cylinder297
  Angle = 360
  AttacherType = Attacher::AttachEngine3D
  FirstAngle = 0
  Height = 3
  Placement = pos=(15,0,0) rot=(0,0,1;0rad)
  Radius = 1.65
  SecondAngle = 0
  expr: .Placement.Base.x = <<BreadboardConfig>>.screw_spacing * 3
  expr: Height = <<BreadboardConfig>>.t_plate
  expr: Radius = <<BreadboardConfig>>.screw_corehole / 2
FEATURE [Part::Cylinder] Cylinder298
  Angle = 360
  AttacherType = Attacher::AttachEngine3D
  FirstAngle = 0
  Height = 3
  Placement = pos=(20,0,0) rot=(0,0,1;0rad)
  Radius = 1.65
  SecondAngle = 0
  expr: .Placement.Base.x = <<BreadboardConfig>>.screw_spacing * 4
  expr: Height = <<BreadboardConfig>>.t_plate
  expr: Radius = <<BreadboardConfig>>.screw_corehole / 2
FEATURE [Part::Cylinder] Cylinder299
  Angle = 360
  AttacherType = Attacher::AttachEngine3D
  FirstAngle = 0
  Height = 3
  Placement = pos=(25,0,0) rot=(0,0,1;0rad)
  Radius = 1.65
  SecondAngle = 0
  expr: .Placement.Base.x = <<BreadboardConfig>>.screw_spacing * 5
  expr: Height = <<BreadboardConfig>>.t_plate
  expr: Radius = <<BreadboardConfig>>.screw_corehole / 2
FEATURE [Part::Cylinder] Cylinder300
  Angle = 360
  AttacherType = Attacher::AttachEngine3D
  FirstAngle = 0
  Height = 3
  Placement = pos=(30,0,0) rot=(0,0,1;0rad)
  Radius = 1.65
  SecondAngle = 0
  expr: .Placement.Base.x = <<BreadboardConfig>>.screw_spacing * 6
  expr: Height = <<BreadboardConfig>>.t_plate
  expr: Radius = <<BreadboardConfig>>.screw_corehole / 2
FEATURE [Part::Cylinder] Cylinder305
  Angle = 360
  AttacherType = Attacher::AttachEngine3D
  FirstAngle = 0
  Height = 3
  Placement = pos=(-5,0,0) rot=(0,0,1;0rad)
  Radius = 1.65
  SecondAngle = 0
  expr: .Placement.Base.x = <<BreadboardConfig>>.screw_spacing * -1
  expr: Height = <<BreadboardConfig>>.t_plate
  expr: Radius = <<BreadboardConfig>>.screw_corehole / 2
FEATURE [Part::Cylinder] Cylinder306
  Angle = 360
  AttacherType = Attacher::AttachEngine3D
  FirstAngle = 0
  Height = 3
  Placement = pos=(-10,0,0) rot=(0,0,1;0rad)
  Radius = 1.65
  SecondAngle = 0
  expr: .Placement.Base.x = <<BreadboardConfig>>.screw_spacing * -2
  expr: Height = <<BreadboardConfig>>.t_plate
  expr: Radius = <<BreadboardConfig>>.screw_corehole / 2
FEATURE [Part::Cylinder] Cylinder307
  Angle = 360
  AttacherType = Attacher::AttachEngine3D
  FirstAngle = 0
  Height = 3
  Placement = pos=(-15,0,0) rot=(0,0,1;0rad)
  Radius = 1.65
  SecondAngle = 0
  expr: .Placement.Base.x = <<BreadboardConfig>>.screw_spacing * -3
  expr: Height = <<BreadboardConfig>>.t_plate
  expr: Radius = <<BreadboardConfig>>.screw_corehole / 2
FEATURE [Part::Cylinder] Cylinder308
  Angle = 360
  AttacherType = Attacher::AttachEngine3D
  FirstAngle = 0
  Height = 3
  Placement = pos=(-20,0,0) rot=(0,0,1;0rad)
  Radius = 1.65
  SecondAngle = 0
  expr: .Placement.Base.x = <<BreadboardConfig>>.screw_spacing * -4
  expr: Height = <<BreadboardConfig>>.t_plate
  expr: Radius = <<BreadboardConfig>>.screw_corehole / 2
FEATURE [Part::Cylinder] Cylinder309
  Angle = 360
  AttacherType = Attacher::AttachEngine3D
  FirstAngle = 0
  Height = 3
  Placement = pos=(-25,0,0) rot=(0,0,1;0rad)
  Radius = 1.65
  SecondAngle = 0
  expr: .Placement.Base.x = <<BreadboardConfig>>.screw_spacing * -5
  expr: Height = <<BreadboardConfig>>.t_plate
  expr: Radius = <<BreadboardConfig>>.screw_corehole / 2
FEATURE [Part::Cylinder] Cylinder310
  Angle = 360
  AttacherType = Attacher::AttachEngine3D
  FirstAngle = 0
  Height = 3
  Placement = pos=(-30,0,0) rot=(0,0,1;0rad)
  Radius = 1.65
  SecondAngle = 0
  expr: .Placement.Base.x = <<BreadboardConfig>>.screw_spacing * -6
  expr: Height = <<BreadboardConfig>>.t_plate
  expr: Radius = <<BreadboardConfig>>.screw_corehole / 2
FEATURE [Part::Cylinder] Cylinder315
  Angle = 360
  AttacherType = Attacher::AttachEngine3D
  FirstAngle = 0
  Height = 3
  Radius = 1.65
  SecondAngle = 0
  expr: Height = <<BreadboardConfig>>.t_plate
  expr: Radius = <<BreadboardConfig>>.screw_corehole / 2
FEATURE [Part::MultiFuse] Fusion015
  Placement = pos=(0,-20,0) rot=(0,0,1;0rad)
  Shapes = -> [Cylinder310,Cylinder309,Cylinder308,Cylinder307,Cylinder306,Cylinder305,Cylinder300,Cylinder299,Cylinder298,Cylinder297,Cylinder296,Cylinder295,Cylinder315]
  expr: .Placement.Base.y = <<BreadboardConfig>>.screw_spacing * -4
FEATURE [Part::Cylinder] Cylinder316
  Angle = 360
  AttacherType = Attacher::AttachEngine3D
  FirstAngle = 0
  Height = 3
  Placement = pos=(5,0,0) rot=(0,0,1;0rad)
  Radius = 1.65
  SecondAngle = 0
  expr: .Placement.Base.x = <<BreadboardConfig>>.screw_spacing * 1
  expr: Height = <<BreadboardConfig>>.t_plate
  expr: Radius = <<BreadboardConfig>>.screw_corehole / 2
FEATURE [Part::Cylinder] Cylinder317
  Angle = 360
  AttacherType = Attacher::AttachEngine3D
  FirstAngle = 0
  Height = 3
  Placement = pos=(10,0,0) rot=(0,0,1;0rad)
  Radius = 1.65
  SecondAngle = 0
  expr: .Placement.Base.x = <<BreadboardConfig>>.screw_spacing * 2
  expr: Height = <<BreadboardConfig>>.t_plate
  expr: Radius = <<BreadboardConfig>>.screw_corehole / 2
FEATURE [Part::Cylinder] Cylinder318
  Angle = 360
  AttacherType = Attacher::AttachEngine3D
  FirstAngle = 0
  Height = 3
  Placement = pos=(15,0,0) rot=(0,0,1;0rad)
  Radius = 1.65
  SecondAngle = 0
  expr: .Placement.Base.x = <<BreadboardConfig>>.screw_spacing * 3
  expr: Height = <<BreadboardConfig>>.t_plate
  expr: Radius = <<BreadboardConfig>>.screw_corehole / 2
FEATURE [Part::Cylinder] Cylinder319
  Angle = 360
  AttacherType = Attacher::AttachEngine3D
  FirstAngle = 0
  Height = 3
  Placement = pos=(20,0,0) rot=(0,0,1;0rad)
  Radius = 1.65
  SecondAngle = 0
  expr: .Placement.Base.x = <<BreadboardConfig>>.screw_spacing * 4
  expr: Height = <<BreadboardConfig>>.t_plate
  expr: Radius = <<BreadboardConfig>>.screw_corehole / 2
FEATURE [Part::Cylinder] Cylinder320
  Angle = 360
  AttacherType = Attacher::AttachEngine3D
  FirstAngle = 0
  Height = 3
  Placement = pos=(25,0,0) rot=(0,0,1;0rad)
  Radius = 1.65
  SecondAngle = 0
  expr: .Placement.Base.x = <<BreadboardConfig>>.screw_spacing * 5
  expr: Height = <<BreadboardConfig>>.t_plate
  expr: Radius = <<BreadboardConfig>>.screw_corehole / 2
FEATURE [Part::Cylinder] Cylinder326
  Angle = 360
  AttacherType = Attacher::AttachEngine3D
  FirstAngle = 0
  Height = 3
  Placement = pos=(-5,0,0) rot=(0,0,1;0rad)
  Radius = 1.65
  SecondAngle = 0
  expr: .Placement.Base.x = <<BreadboardConfig>>.screw_spacing * -1
  expr: Height = <<BreadboardConfig>>.t_plate
  expr: Radius = <<BreadboardConfig>>.screw_corehole / 2
FEATURE [Part::Cylinder] Cylinder327
  Angle = 360
  AttacherType = Attacher::AttachEngine3D
  FirstAngle = 0
  Height = 3
  Placement = pos=(-10,0,0) rot=(0,0,1;0rad)
  Radius = 1.65
  SecondAngle = 0
  expr: .Placement.Base.x = <<BreadboardConfig>>.screw_spacing * -2
  expr: Height = <<BreadboardConfig>>.t_plate
  expr: Radius = <<BreadboardConfig>>.screw_corehole / 2
FEATURE [Part::Cylinder] Cylinder328
  Angle = 360
  AttacherType = Attacher::AttachEngine3D
  FirstAngle = 0
  Height = 3
  Placement = pos=(-15,0,0) rot=(0,0,1;0rad)
  Radius = 1.65
  SecondAngle = 0
  expr: .Placement.Base.x = <<BreadboardConfig>>.screw_spacing * -3
  expr: Height = <<BreadboardConfig>>.t_plate
  expr: Radius = <<BreadboardConfig>>.screw_corehole / 2
FEATURE [Part::Cylinder] Cylinder329
  Angle = 360
  AttacherType = Attacher::AttachEngine3D
  FirstAngle = 0
  Height = 3
  Placement = pos=(-20,0,0) rot=(0,0,1;0rad)
  Radius = 1.65
  SecondAngle = 0
  expr: .Placement.Base.x = <<BreadboardConfig>>.screw_spacing * -4
  expr: Height = <<BreadboardConfig>>.t_plate
  expr: Radius = <<BreadboardConfig>>.screw_corehole / 2
FEATURE [Part::Cylinder] Cylinder330
  Angle = 360
  AttacherType = Attacher::AttachEngine3D
  FirstAngle = 0
  Height = 3
  Placement = pos=(-25,0,0) rot=(0,0,1;0rad)
  Radius = 1.65
  SecondAngle = 0
  expr: .Placement.Base.x = <<BreadboardConfig>>.screw_spacing * -5
  expr: Height = <<BreadboardConfig>>.t_plate
  expr: Radius = <<BreadboardConfig>>.screw_corehole / 2
FEATURE [Part::Cylinder] Cylinder336
  Angle = 360
  AttacherType = Attacher::AttachEngine3D
  FirstAngle = 0
  Height = 3
  Radius = 1.65
  SecondAngle = 0
  expr: Height = <<BreadboardConfig>>.t_plate
  expr: Radius = <<BreadboardConfig>>.screw_corehole / 2
FEATURE [Part::MultiFuse] Fusion016
  Placement = pos=(0,-25,0) rot=(0,0,1;0rad)
  Shapes = -> [Cylinder330,Cylinder329,Cylinder328,Cylinder327,Cylinder326,Cylinder320,Cylinder319,Cylinder318,Cylinder317,Cylinder316,Cylinder336]
  expr: .Placement.Base.y = <<BreadboardConfig>>.screw_spacing * -5
FEATURE [Part::Cylinder] Cylinder337
  Angle = 360
  AttacherType = Attacher::AttachEngine3D
  FirstAngle = 0
  Height = 3
  Placement = pos=(5,0,0) rot=(0,0,1;0rad)
  Radius = 1.65
  SecondAngle = 0
  expr: .Placement.Base.x = <<BreadboardConfig>>.screw_spacing * 1
  expr: Height = <<BreadboardConfig>>.t_plate
  expr: Radius = <<BreadboardConfig>>.screw_corehole / 2
FEATURE [Part::Cylinder] Cylinder338
  Angle = 360
  AttacherType = Attacher::AttachEngine3D
  FirstAngle = 0
  Height = 3
  Placement = pos=(10,0,0) rot=(0,0,1;0rad)
  Radius = 1.65
  SecondAngle = 0
  expr: .Placement.Base.x = <<BreadboardConfig>>.screw_spacing * 2
  expr: Height = <<BreadboardConfig>>.t_plate
  expr: Radius = <<BreadboardConfig>>.screw_corehole / 2
FEATURE [Part::Cylinder] Cylinder339
  Angle = 360
  AttacherType = Attacher::AttachEngine3D
  FirstAngle = 0
  Height = 3
  Placement = pos=(15,0,0) rot=(0,0,1;0rad)
  Radius = 1.65
  SecondAngle = 0
  expr: .Placement.Base.x = <<BreadboardConfig>>.screw_spacing * 3
  expr: Height = <<BreadboardConfig>>.t_plate
  expr: Radius = <<BreadboardConfig>>.screw_corehole / 2
FEATURE [Part::Cylinder] Cylinder340
  Angle = 360
  AttacherType = Attacher::AttachEngine3D
  FirstAngle = 0
  Height = 3
  Placement = pos=(20,0,0) rot=(0,0,1;0rad)
  Radius = 1.65
  SecondAngle = 0
  expr: .Placement.Base.x = <<BreadboardConfig>>.screw_spacing * 4
  expr: Height = <<BreadboardConfig>>.t_plate
  expr: Radius = <<BreadboardConfig>>.screw_corehole / 2
FEATURE [Part::Cylinder] Cylinder347
  Angle = 360
  AttacherType = Attacher::AttachEngine3D
  FirstAngle = 0
  Height = 3
  Placement = pos=(-5,0,0) rot=(0,0,1;0rad)
  Radius = 1.65
  SecondAngle = 0
  expr: .Placement.Base.x = <<BreadboardConfig>>.screw_spacing * -1
  expr: Height = <<BreadboardConfig>>.t_plate
  expr: Radius = <<BreadboardConfig>>.screw_corehole / 2
FEATURE [Part::Cylinder] Cylinder348
  Angle = 360
  AttacherType = Attacher::AttachEngine3D
  FirstAngle = 0
  Height = 3
  Placement = pos=(-10,0,0) rot=(0,0,1;0rad)
  Radius = 1.65
  SecondAngle = 0
  expr: .Placement.Base.x = <<BreadboardConfig>>.screw_spacing * -2
  expr: Height = <<BreadboardConfig>>.t_plate
  expr: Radius = <<BreadboardConfig>>.screw_corehole / 2
FEATURE [Part::Cylinder] Cylinder349
  Angle = 360
  AttacherType = Attacher::AttachEngine3D
  FirstAngle = 0
  Height = 3
  Placement = pos=(-15,0,0) rot=(0,0,1;0rad)
  Radius = 1.65
  SecondAngle = 0
  expr: .Placement.Base.x = <<BreadboardConfig>>.screw_spacing * -3
  expr: Height = <<BreadboardConfig>>.t_plate
  expr: Radius = <<BreadboardConfig>>.screw_corehole / 2
FEATURE [Part::Cylinder] Cylinder350
  Angle = 360
  AttacherType = Attacher::AttachEngine3D
  FirstAngle = 0
  Height = 3
  Placement = pos=(-20,0,0) rot=(0,0,1;0rad)
  Radius = 1.65
  SecondAngle = 0
  expr: .Placement.Base.x = <<BreadboardConfig>>.screw_spacing * -4
  expr: Height = <<BreadboardConfig>>.t_plate
  expr: Radius = <<BreadboardConfig>>.screw_corehole / 2
FEATURE [Part::Cylinder] Cylinder357
  Angle = 360
  AttacherType = Attacher::AttachEngine3D
  FirstAngle = 0
  Height = 3
  Radius = 1.65
  SecondAngle = 0
  expr: Height = <<BreadboardConfig>>.t_plate
  expr: Radius = <<BreadboardConfig>>.screw_corehole / 2
FEATURE [Part::MultiFuse] Fusion017
  Placement = pos=(0,-30,0) rot=(0,0,1;0rad)
  Shapes = -> [Cylinder350,Cylinder349,Cylinder348,Cylinder347,Cylinder340,Cylinder339,Cylinder338,Cylinder337,Cylinder357]
  expr: .Placement.Base.y = <<BreadboardConfig>>.screw_spacing * -6
FEATURE [Part::Cylinder] Cylinder421
  Angle = 360
  AttacherType = Attacher::AttachEngine3D
  FirstAngle = 0
  Height = 3
  Placement = pos=(5,0,0) rot=(0,0,1;0rad)
  Radius = 1.65
  SecondAngle = 0
  expr: .Placement.Base.x = <<BreadboardConfig>>.screw_spacing * 1
  expr: Height = <<BreadboardConfig>>.t_plate
  expr: Radius = <<BreadboardConfig>>.screw_corehole / 2
FEATURE [Part::Cylinder] Cylinder422
  Angle = 360
  AttacherType = Attacher::AttachEngine3D
  FirstAngle = 0
  Height = 3
  Placement = pos=(10,0,0) rot=(0,0,1;0rad)
  Radius = 1.65
  SecondAngle = 0
  expr: .Placement.Base.x = <<BreadboardConfig>>.screw_spacing * 2
  expr: Height = <<BreadboardConfig>>.t_plate
  expr: Radius = <<BreadboardConfig>>.screw_corehole / 2
FEATURE [Part::Cylinder] Cylinder431
  Angle = 360
  AttacherType = Attacher::AttachEngine3D
  FirstAngle = 0
  Height = 3
  Placement = pos=(-5,0,0) rot=(0,0,1;0rad)
  Radius = 1.65
  SecondAngle = 0
  expr: .Placement.Base.x = <<BreadboardConfig>>.screw_spacing * -1
  expr: Height = <<BreadboardConfig>>.t_plate
  expr: Radius = <<BreadboardConfig>>.screw_corehole / 2
FEATURE [Part::Cylinder] Cylinder432
  Angle = 360
  AttacherType = Attacher::AttachEngine3D
  FirstAngle = 0
  Height = 3
  Placement = pos=(-10,0,0) rot=(0,0,1;0rad)
  Radius = 1.65
  SecondAngle = 0
  expr: .Placement.Base.x = <<BreadboardConfig>>.screw_spacing * -2
  expr: Height = <<BreadboardConfig>>.t_plate
  expr: Radius = <<BreadboardConfig>>.screw_corehole / 2
FEATURE [Part::Cylinder] Cylinder441
  Angle = 360
  AttacherType = Attacher::AttachEngine3D
  FirstAngle = 0
  Height = 3
  Radius = 1.65
  SecondAngle = 0
  expr: Height = <<BreadboardConfig>>.t_plate
  expr: Radius = <<BreadboardConfig>>.screw_corehole / 2
FEATURE [Part::MultiFuse] Fusion022
  Placement = pos=(0,-35,0) rot=(0,0,1;0rad)
  Shapes = -> [Cylinder432,Cylinder431,Cylinder422,Cylinder421,Cylinder441]
  expr: .Placement.Base.y = <<BreadboardConfig>>.screw_spacing * -7
FEATURE [Part::Cylinder] Cylinder025
  Angle = 360
  AttacherType = Attacher::AttachEngine3D
  FirstAngle = 0
  Height = 3
  Placement = pos=(20,0,0) rot=(0,0,1;0rad)
  Radius = 1.65
  SecondAngle = 0
  expr: .Placement.Base.x = <<BreadboardConfig>>.screw_spacing * 4
  expr: Height = <<BreadboardConfig>>.t_plate
  expr: Radius = <<BreadboardConfig>>.screw_corehole / 2
FEATURE [Part::Cylinder] Cylinder026
  Angle = 360
  AttacherType = Attacher::AttachEngine3D
  FirstAngle = 0
  Height = 3
  Placement = pos=(25,0,0) rot=(0,0,1;0rad)
  Radius = 1.65
  SecondAngle = 0
  expr: .Placement.Base.x = <<BreadboardConfig>>.screw_spacing * 5
  expr: Height = <<BreadboardConfig>>.t_plate
  expr: Radius = <<BreadboardConfig>>.screw_corehole / 2
FEATURE [Part::Cylinder] Cylinder027
  Angle = 360
  AttacherType = Attacher::AttachEngine3D
  FirstAngle = 0
  Height = 3
  Placement = pos=(30,0,0) rot=(0,0,1;0rad)
  Radius = 1.65
  SecondAngle = 0
  expr: .Placement.Base.x = <<BreadboardConfig>>.screw_spacing * 6
  expr: Height = <<BreadboardConfig>>.t_plate
  expr: Radius = <<BreadboardConfig>>.screw_corehole / 2
FEATURE [Part::Cylinder] Cylinder028
  Angle = 360
  AttacherType = Attacher::AttachEngine3D
  FirstAngle = 0
  Height = 3
  Placement = pos=(35,0,0) rot=(0,0,1;0rad)
  Radius = 1.65
  SecondAngle = 0
  expr: .Placement.Base.x = <<BreadboardConfig>>.screw_spacing * 7
  expr: Height = <<BreadboardConfig>>.t_plate
  expr: Radius = <<BreadboardConfig>>.screw_corehole / 2
FEATURE [Part::Cylinder] Cylinder035
  Angle = 360
  AttacherType = Attacher::AttachEngine3D
  FirstAngle = 0
  Height = 3
  Placement = pos=(-20,0,0) rot=(0,0,1;0rad)
  Radius = 1.65
  SecondAngle = 0
  expr: .Placement.Base.x = <<BreadboardConfig>>.screw_spacing * -4
  expr: Height = <<BreadboardConfig>>.t_plate
  expr: Radius = <<BreadboardConfig>>.screw_corehole / 2
FEATURE [Part::Cylinder] Cylinder036
  Angle = 360
  AttacherType = Attacher::AttachEngine3D
  FirstAngle = 0
  Height = 3
  Placement = pos=(-25,0,0) rot=(0,0,1;0rad)
  Radius = 1.65
  SecondAngle = 0
  expr: .Placement.Base.x = <<BreadboardConfig>>.screw_spacing * -5
  expr: Height = <<BreadboardConfig>>.t_plate
  expr: Radius = <<BreadboardConfig>>.screw_corehole / 2
FEATURE [Part::Cylinder] Cylinder037
  Angle = 360
  AttacherType = Attacher::AttachEngine3D
  FirstAngle = 0
  Height = 3
  Placement = pos=(-30,0,0) rot=(0,0,1;0rad)
  Radius = 1.65
  SecondAngle = 0
  expr: .Placement.Base.x = <<BreadboardConfig>>.screw_spacing * -6
  expr: Height = <<BreadboardConfig>>.t_plate
  expr: Radius = <<BreadboardConfig>>.screw_corehole / 2
FEATURE [Part::Cylinder] Cylinder038
  Angle = 360
  AttacherType = Attacher::AttachEngine3D
  FirstAngle = 0
  Height = 3
  Placement = pos=(-35,0,0) rot=(0,0,1;0rad)
  Radius = 1.65
  SecondAngle = 0
  expr: .Placement.Base.x = <<BreadboardConfig>>.screw_spacing * -7
  expr: Height = <<BreadboardConfig>>.t_plate
  expr: Radius = <<BreadboardConfig>>.screw_corehole / 2
FEATURE [Part::MultiFuse] Fusion002
  Placement = pos=(0,5,0) rot=(0,0,1;0rad)
  Shapes = -> [Cylinder038,Cylinder037,Cylinder036,Cylinder035,Cylinder034,Cylinder033,Cylinder032,Cylinder028,Cylinder027,Cylinder026,Cylinder025,Cylinder024,Cylinder023,Cylinder022,Cylinder042]
  expr: .Placement.Base.y = <<BreadboardConfig>>.screw_spacing
FEATURE [Part::MultiFuse] Fusion021  label="HoleMatrix"
  Shapes = -> [Fusion003,Fusion004,Fusion005,Fusion006,Fusion007,Fusion008,Fusion012,Fusion013,Fusion014,Fusion015,Fusion016,Fusion017,Fusion002,Fusion001,Fusion022]
FEATURE [Part::Cut] Cut
  Base = -> Fusion
  Tool = -> Fusion021
FEATURE [TechDraw::DrawSVGTemplate] Template
  EditableTexts = Designed_by_Name=Thomas Spielauer; FC-Date=2024-01-29; FC-SC=mm; FC-Title=XL30 Stage Breadboard; Subtitle=80mm OD, M4 threads, Aluminum
  Height = 210
  Orientation = 1
  Template = <path>
  Width = 297
FEATURE [TechDraw::DrawProjGroupItem] ProjItem  label="Front"
  CoarseView = false
  Direction = (0,0,1)
  Focus = 100
  HardHidden = false
  IsoCount = 0
  IsoHidden = false
  IsoVisible = false
  LockPosition = true
  Perspective = false
  Rotation = 0
  RotationVector = (0,-1,0)
  Scale = 1.5
  ScaleType = 2
  ScrubCount = 0
  SeamHidden = false
  SeamVisible = false
  SmoothHidden = false
  SmoothVisible = true
  Source = -> [Cut]
  Type = 0
  X = 0
  XDirection = (0,-1,0)
  Y = 0
FEATURE [TechDraw::DrawProjGroupItem] ProjItem001  label="Left"
  CoarseView = false
  Direction = (0,1,1e-16)
  Focus = 100
  HardHidden = false
  IsoCount = 0
  IsoHidden = false
  IsoVisible = false
  LockPosition = false
  Perspective = false
  Rotation = 0
  RotationVector = (1,0,0)
  Scale = 1.5
  ScaleType = 2
  ScrubCount = 0
  SeamHidden = false
  SeamVisible = false
  SmoothHidden = false
  SmoothVisible = true
  Source = -> [Cut]
  Type = 1
  X = 142.5
  XDirection = (0,-1e-16,1)
  Y = 0
FEATURE [TechDraw::DrawProjGroupItem] ProjItem002  label="Top"
  CoarseView = false
  Direction = (1,0,0)
  Focus = 100
  HardHidden = false
  IsoCount = 0
  IsoHidden = false
  IsoVisible = false
  LockPosition = false
  Perspective = false
  Rotation = 0
  RotationVector = (1,0,0)
  Scale = 1.5
  ScaleType = 2
  ScrubCount = 0
  SeamHidden = false
  SeamVisible = false
  SmoothHidden = false
  SmoothVisible = true
  Source = -> [Cut]
  Type = 4
  X = 0
  XDirection = (0,-1,0)
  Y = -96.0655
FEATURE [TechDraw::DrawProjGroup] ProjGroup
  Anchor = -> ProjItem
  AutoDistribute = false
  LockPosition = false
  ProjectionType = 0
  Rotation = 0
  Scale = 1.5
  ScaleType = 2
  Source = -> [Cut]
  Views = -> [ProjItem,ProjItem001,ProjItem002]
  X = 80.3073
  Y = 132.993
  spacingX = 15
  spacingY = 15
FEATURE [TechDraw::DrawViewDimension] Dimension001
  AngleOverride = false
  Arbitrary = false
  ArbitraryTolerances = false
  EqualTolerance = true
  ExtensionAngle = 0
  FormatSpec = %.2w
  FormatSpecOverTolerance = %+.2w
  FormatSpecUnderTolerance = %+.2w
  Inverted = false
  LineAngle = 0
  LockPosition = false
  MeasureType = 1
  OverTolerance = 0
  References2D = -> [ProjItem001]
  Rotation = 0
  ScaleType = 0
  TheoreticalExact = false
  Type = 2
  UnderTolerance = 0
  X = 23.5605
  Y = 2.43727
FEATURE [TechDraw::DrawViewDimension] Dimension
  AngleOverride = false
  Arbitrary = false
  ArbitraryTolerances = false
  EqualTolerance = true
  ExtensionAngle = 0
  FormatSpec = %.2w
  FormatSpecOverTolerance = %+.2w
  FormatSpecUnderTolerance = %+.2w
  Inverted = false
  LineAngle = 0
  LockPosition = false
  MeasureType = 1
  OverTolerance = 0
  References2D = -> [ProjItem001]
  Rotation = 0
  ScaleType = 0
  TheoreticalExact = false
  Type = 0
  UnderTolerance = 0
  X = 12.7358
  Y = -62.9896
FEATURE [TechDraw::DrawViewDimension] Dimension002
  AngleOverride = false
  Arbitrary = false
  ArbitraryTolerances = false
  EqualTolerance = true
  ExtensionAngle = 0
  FormatSpec = %.2w
  FormatSpecOverTolerance = %+.2w
  FormatSpecUnderTolerance = %+.2w
  Inverted = false
  LineAngle = 0
  LockPosition = false
  MeasureType = 1
  OverTolerance = 0
  References2D = -> [ProjItem001]
  Rotation = 0
  ScaleType = 0
  TheoreticalExact = false
  Type = 0
  UnderTolerance = 0
  X = -16.294
  Y = -9.39958
FEATURE [TechDraw::DrawViewDimension] Dimension003
  AngleOverride = false
  Arbitrary = false
  ArbitraryTolerances = false
  EqualTolerance = true
  ExtensionAngle = 0
  FormatSpec = %.2w (M4)
  FormatSpecOverTolerance = %+.2w
  FormatSpecUnderTolerance = %+.2w
  Inverted = false
  LineAngle = 0
  LockPosition = false
  MeasureType = 1
  OverTolerance = 0
  References2D = -> [ProjItem001]
  Rotation = 0
  ScaleType = 0
  TheoreticalExact = false
  Type = 0
  UnderTolerance = 0
  X = -23.6925
  Y = 24.5282
FEATURE [TechDraw::DrawViewDimension] Dimension004
  AngleOverride = false
  Arbitrary = false
  ArbitraryTolerances = false
  EqualTolerance = true
  ExtensionAngle = 0
  FormatSpec = %.2w
  FormatSpecOverTolerance = %+.2w
  FormatSpecUnderTolerance = %+.2w
  Inverted = false
  LineAngle = 0
  LockPosition = false
  MeasureType = 1
  OverTolerance = 0
  References2D = -> [ProjItem]
  Rotation = 0
  ScaleType = 0
  TheoreticalExact = false
  Type = 0
  UnderTolerance = 0
  X = 26.0636
  Y = 64.7425
FEATURE [TechDraw::DrawViewDimension] Dimension005
  AngleOverride = false
  Arbitrary = false
  ArbitraryTolerances = false
  EqualTolerance = true
  ExtensionAngle = 0
  FormatSpec = %.2w
  FormatSpecOverTolerance = %+.2w
  FormatSpecUnderTolerance = %+.2w
  Inverted = false
  LineAngle = 0
  LockPosition = false
  MeasureType = 1
  OverTolerance = 0
  References2D = -> [ProjItem]
  Rotation = 0
  ScaleType = 0
  TheoreticalExact = false
  Type = 0
  UnderTolerance = 0
  X = 51.9554
  Y = 60.6364
FEATURE [TechDraw::DrawViewDimension] Dimension006
  AngleOverride = false
  Arbitrary = false
  ArbitraryTolerances = false
  EqualTolerance = true
  ExtensionAngle = 0
  FormatSpec = ⌀%.2w (176x M4)
  FormatSpecOverTolerance = %+.2w
  FormatSpecUnderTolerance = %+.2w
  Inverted = false
  LineAngle = 0
  LockPosition = false
  MeasureType = 1
  OverTolerance = 0
  References2D = -> [ProjItem]
  Rotation = 0
  ScaleType = 0
  TheoreticalExact = false
  Type = 5
  UnderTolerance = 0
  X = 77.132
  Y = 37.3294
FEATURE [TechDraw::DrawPage] Page
  KeepUpdated = true
  NextBalloonIndex = 1
  ProjectionType = 0
  Template = -> Template
  Views = -> [ProjGroup,Dimension001,Dimension,Dimension002,Dimension003,Dimension004,Dimension005,Dimension006]
note: 1 file-system path scrubbed to <path> (originals preserved in the JSON sidecar)
